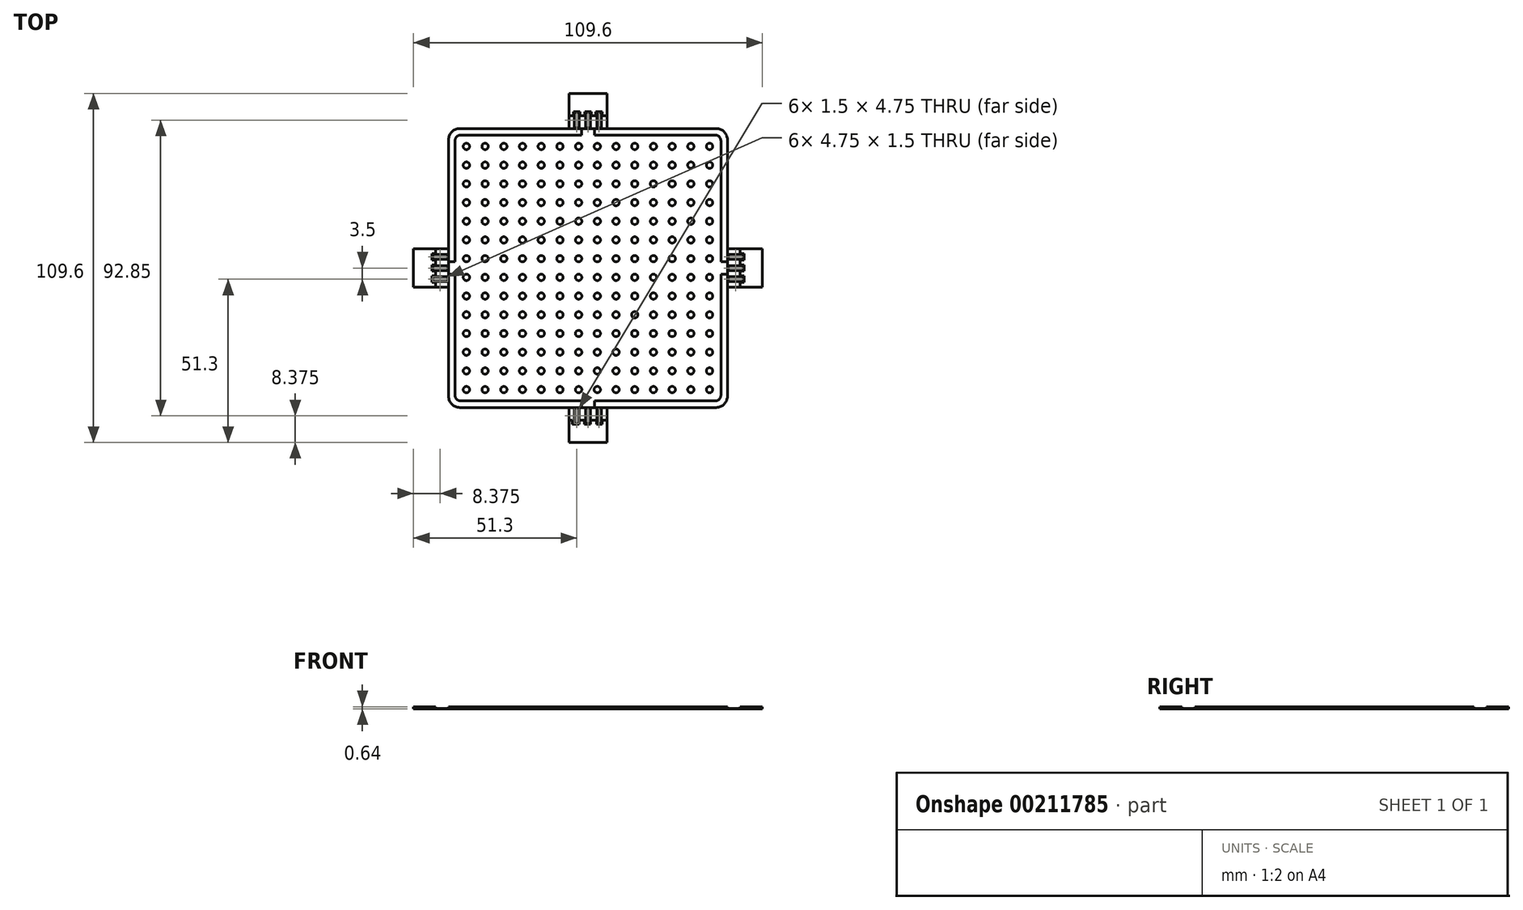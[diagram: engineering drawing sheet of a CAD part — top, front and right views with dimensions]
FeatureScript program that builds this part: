
annotation { "Feature Type Name" : "Feature", "Feature Type Description" : "" }
export const myFeature = defineFeature(function(context is Context, id is Id, definition is map)
    precondition{}
    {
        {
            var Q0;
            Q0=qCreatedBy(makeId("Top.planeOp"),FACE);
            var sketch = newSketch(context, id + "F0", { "sketchPlane" : qUnion([Q0])});
            skLineSegment(sketch, "E0.bottom", {"start": v(3.5, 87.6) * mm, "end": v(37.8, 87.6) * mm});
            skLineSegment(sketch, "E0.top", {"start": v(3.5, 0) * mm, "end": v(37.8, 0) * mm});
            skLineSegment(sketch, "E0.left", {"start": v(0, 84.1) * mm, "end": v(0, 49.8) * mm});
            skLineSegment(sketch, "E0.right", {"start": v(87.6, 84.1) * mm, "end": v(87.6, 49.8) * mm});
            skLineSegment(sketch, "E1", {"start": v(37.8, 87.6) * mm, "end": v(37.8, 98.6) * mm});
            skLineSegment(sketch, "E2", {"start": v(37.8, 98.6) * mm, "end": v(49.8, 98.6) * mm});
            skLineSegment(sketch, "E3", {"start": v(49.8, 98.6) * mm, "end": v(49.8, 87.6) * mm});
            skLineSegment(sketch, "E4.trimOffspring", {"start": v(49.8, 87.6) * mm, "end": v(84.1, 87.6) * mm});
            skLineSegment(sketch, "E5", {"start": v(87.6, 49.8) * mm, "end": v(98.6, 49.8) * mm});
            skLineSegment(sketch, "E6", {"start": v(98.6, 49.8) * mm, "end": v(98.6, 37.8) * mm});
            skLineSegment(sketch, "E7", {"start": v(98.6, 37.8) * mm, "end": v(87.6, 37.8) * mm});
            skLineSegment(sketch, "E8.trimOffspring", {"start": v(87.6, 37.8) * mm, "end": v(87.6, 3.5) * mm});
            skLineSegment(sketch, "E9", {"start": v(49.8, 0) * mm, "end": v(49.8, -11) * mm});
            skLineSegment(sketch, "E10", {"start": v(49.8, -11) * mm, "end": v(37.8, -11) * mm});
            skLineSegment(sketch, "E11", {"start": v(37.8, -11) * mm, "end": v(37.8, 0) * mm});
            skLineSegment(sketch, "E12.trimOffspring", {"start": v(49.8, 0) * mm, "end": v(84.1, 0) * mm});
            skLineSegment(sketch, "E13", {"start": v(0, 49.8) * mm, "end": v(-11, 49.8) * mm});
            skLineSegment(sketch, "E14", {"start": v(-11, 49.8) * mm, "end": v(-11, 37.8) * mm});
            skLineSegment(sketch, "E15", {"start": v(-11, 37.8) * mm, "end": v(0, 37.8) * mm});
            skLineSegment(sketch, "E16.trimOffspring", {"start": v(0, 37.8) * mm, "end": v(0, 3.5) * mm});
            skLineSegment(sketch, "E17.bottom", {"start": v(41.05, 87.85) * mm, "end": v(39.55, 87.85) * mm});
            skLineSegment(sketch, "E17.top", {"start": v(41.05, 92.6) * mm, "end": v(39.55, 92.6) * mm});
            skLineSegment(sketch, "E17.left", {"start": v(41.05, 87.85) * mm, "end": v(41.05, 92.6) * mm});
            skLineSegment(sketch, "E17.right", {"start": v(39.55, 87.85) * mm, "end": v(39.55, 92.6) * mm});
            skPoint(sketch, "E17.middle", {"position": v(40.3, 90.22) * mm});
            skLineSegment(sketch, "E18.1.0.0", {"start": v(44.55, 92.6) * mm, "end": v(43.05, 92.6) * mm});
            skLineSegment(sketch, "E18.1.0.1", {"start": v(44.55, 87.85) * mm, "end": v(44.55, 92.6) * mm});
            skLineSegment(sketch, "E18.1.0.2", {"start": v(44.55, 87.85) * mm, "end": v(43.05, 87.85) * mm});
            skLineSegment(sketch, "E18.1.0.3", {"start": v(43.05, 87.85) * mm, "end": v(43.05, 92.6) * mm});
            skPoint(sketch, "E18.1.0.4", {"position": v(43.8, 90.22) * mm});
            skLineSegment(sketch, "E18.2.0.0", {"start": v(48.05, 92.6) * mm, "end": v(46.55, 92.6) * mm});
            skLineSegment(sketch, "E18.2.0.1", {"start": v(48.05, 87.85) * mm, "end": v(48.05, 92.6) * mm});
            skLineSegment(sketch, "E18.2.0.2", {"start": v(48.05, 87.85) * mm, "end": v(46.55, 87.85) * mm});
            skLineSegment(sketch, "E18.2.0.3", {"start": v(46.55, 87.85) * mm, "end": v(46.55, 92.6) * mm});
            skPoint(sketch, "E18.2.0.4", {"position": v(47.3, 90.22) * mm});
            skLineSegment(sketch, "E18.direction1", {"start": v(39.55, 92.6) * mm, "end": v(43.05, 92.6) * mm, "construction": true});
            skLineSegment(sketch, "E19.bottom", {"start": v(92.6, 46.55) * mm, "end": v(87.85, 46.55) * mm});
            skLineSegment(sketch, "E19.top", {"start": v(92.6, 48.05) * mm, "end": v(87.85, 48.05) * mm});
            skLineSegment(sketch, "E19.left", {"start": v(92.6, 46.55) * mm, "end": v(92.6, 48.05) * mm});
            skLineSegment(sketch, "E19.right", {"start": v(87.85, 46.55) * mm, "end": v(87.85, 48.05) * mm});
            skPoint(sketch, "E19.middle", {"position": v(90.22, 47.3) * mm});
            skLineSegment(sketch, "E20.0.1.0", {"start": v(92.6, 43.05) * mm, "end": v(92.6, 44.55) * mm});
            skLineSegment(sketch, "E20.0.1.1", {"start": v(92.6, 44.55) * mm, "end": v(87.85, 44.55) * mm});
            skLineSegment(sketch, "E20.0.1.2", {"start": v(87.85, 43.05) * mm, "end": v(87.85, 44.55) * mm});
            skLineSegment(sketch, "E20.0.1.3", {"start": v(92.6, 43.05) * mm, "end": v(87.85, 43.05) * mm});
            skPoint(sketch, "E20.0.1.4", {"position": v(90.22, 43.8) * mm});
            skLineSegment(sketch, "E20.0.2.0", {"start": v(92.6, 39.55) * mm, "end": v(92.6, 41.05) * mm});
            skLineSegment(sketch, "E20.0.2.1", {"start": v(92.6, 41.05) * mm, "end": v(87.85, 41.05) * mm});
            skLineSegment(sketch, "E20.0.2.2", {"start": v(87.85, 39.55) * mm, "end": v(87.85, 41.05) * mm});
            skLineSegment(sketch, "E20.0.2.3", {"start": v(92.6, 39.55) * mm, "end": v(87.85, 39.55) * mm});
            skPoint(sketch, "E20.0.2.4", {"position": v(90.22, 40.3) * mm});
            skLineSegment(sketch, "E20.direction1", {"start": v(92.6, 46.55) * mm, "end": v(117.6, 46.55) * mm, "construction": true});
            skLineSegment(sketch, "E20.direction2", {"start": v(92.6, 46.55) * mm, "end": v(92.6, 43.05) * mm, "construction": true});
            skLineSegment(sketch, "E21.bottom", {"start": v(48.05, -5) * mm, "end": v(46.55, -5) * mm});
            skLineSegment(sketch, "E21.top", {"start": v(48.05, -0.25) * mm, "end": v(46.55, -0.25) * mm});
            skLineSegment(sketch, "E21.left", {"start": v(48.05, -5) * mm, "end": v(48.05, -0.25) * mm});
            skLineSegment(sketch, "E21.right", {"start": v(46.55, -5) * mm, "end": v(46.55, -0.25) * mm});
            skPoint(sketch, "E21.middle", {"position": v(47.3, -2.62) * mm});
            skLineSegment(sketch, "E22.1.0.0", {"start": v(44.55, -0.25) * mm, "end": v(43.05, -0.25) * mm});
            skLineSegment(sketch, "E22.1.0.1", {"start": v(44.55, -5) * mm, "end": v(44.55, -0.25) * mm});
            skLineSegment(sketch, "E22.1.0.2", {"start": v(44.55, -5) * mm, "end": v(43.05, -5) * mm});
            skLineSegment(sketch, "E22.1.0.3", {"start": v(43.05, -5) * mm, "end": v(43.05, -0.25) * mm});
            skPoint(sketch, "E22.1.0.4", {"position": v(43.8, -2.62) * mm});
            skLineSegment(sketch, "E22.2.0.0", {"start": v(41.05, -0.25) * mm, "end": v(39.55, -0.25) * mm});
            skLineSegment(sketch, "E22.2.0.1", {"start": v(41.05, -5) * mm, "end": v(41.05, -0.25) * mm});
            skLineSegment(sketch, "E22.2.0.2", {"start": v(41.05, -5) * mm, "end": v(39.55, -5) * mm});
            skLineSegment(sketch, "E22.2.0.3", {"start": v(39.55, -5) * mm, "end": v(39.55, -0.25) * mm});
            skPoint(sketch, "E22.2.0.4", {"position": v(40.3, -2.62) * mm});
            skLineSegment(sketch, "E22.direction1", {"start": v(46.55, -0.25) * mm, "end": v(43.05, -0.25) * mm, "construction": true});
            skLineSegment(sketch, "E23.bottom", {"start": v(-0.25, 46.55) * mm, "end": v(-5, 46.55) * mm});
            skLineSegment(sketch, "E23.top", {"start": v(-0.25, 48.05) * mm, "end": v(-5, 48.05) * mm});
            skLineSegment(sketch, "E23.left", {"start": v(-0.25, 46.55) * mm, "end": v(-0.25, 48.05) * mm});
            skLineSegment(sketch, "E23.right", {"start": v(-5, 46.55) * mm, "end": v(-5, 48.05) * mm});
            skPoint(sketch, "E23.middle", {"position": v(-2.63, 47.3) * mm});
            skLineSegment(sketch, "E24.0.1.0", {"start": v(-0.25, 43.05) * mm, "end": v(-0.25, 44.55) * mm});
            skLineSegment(sketch, "E24.0.1.1", {"start": v(-0.25, 44.55) * mm, "end": v(-5, 44.55) * mm});
            skLineSegment(sketch, "E24.0.1.2", {"start": v(-5, 43.05) * mm, "end": v(-5, 44.55) * mm});
            skPoint(sketch, "E24.0.1.3", {"position": v(-2.63, 43.8) * mm});
            skLineSegment(sketch, "E24.0.1.4", {"start": v(-0.25, 43.05) * mm, "end": v(-5, 43.05) * mm});
            skLineSegment(sketch, "E24.0.2.0", {"start": v(-0.25, 39.55) * mm, "end": v(-0.25, 41.05) * mm});
            skLineSegment(sketch, "E24.0.2.1", {"start": v(-0.25, 41.05) * mm, "end": v(-5, 41.05) * mm});
            skLineSegment(sketch, "E24.0.2.2", {"start": v(-5, 39.55) * mm, "end": v(-5, 41.05) * mm});
            skPoint(sketch, "E24.0.2.3", {"position": v(-2.63, 40.3) * mm});
            skLineSegment(sketch, "E24.0.2.4", {"start": v(-0.25, 39.55) * mm, "end": v(-5, 39.55) * mm});
            skLineSegment(sketch, "E24.direction1", {"start": v(-0.25, 46.55) * mm, "end": v(24.75, 46.55) * mm, "construction": true});
            skLineSegment(sketch, "E24.direction2", {"start": v(-0.25, 46.55) * mm, "end": v(-0.25, 43.05) * mm, "construction": true});
            skPoint(sketch, "E25.visualSharp", {"position": v(0, 87.6) * mm});
            skArc(sketch, "E25.filletArc", {"start": v(3.5, 87.6) * mm, "mid": v(1.03, 86.57) * mm, "end": v(0, 84.1) * mm});
            skPoint(sketch, "E26.visualSharp", {"position": v(87.6, 87.6) * mm});
            skArc(sketch, "E26.filletArc", {"start": v(87.6, 84.1) * mm, "mid": v(86.57, 86.57) * mm, "end": v(84.1, 87.6) * mm});
            skPoint(sketch, "E27.visualSharp", {"position": v(87.6, 0) * mm});
            skArc(sketch, "E27.filletArc", {"start": v(84.1, 0) * mm, "mid": v(86.57, 1.03) * mm, "end": v(87.6, 3.5) * mm});
            skPoint(sketch, "E28.visualSharp", {"position": v(0, 0) * mm});
            skArc(sketch, "E28.filletArc", {"start": v(0, 3.5) * mm, "mid": v(1.03, 1.03) * mm, "end": v(3.5, 0) * mm});
            skSolve(sketch);
        }
        {
            var Q0;
            Q0=makeQuery(id+"F0.imprint","IMPRINT",FACE,{"disambiguationData":[TD([[makeQuery(id+"F0.imprint","IMPRINT",EDGE,{"derivedFrom":sQuery(id+"F0.wireOp",EDGE,"E0.bottom")}),-1.0]])]});
            extrude(context, id + "F1", {"entities" : qUnion([Q0]), "oppositeDirection" : true, "depth" : .127 * mm});
        }
        {
            var Q0;
            Q0=qCreatedBy(makeId("Top.planeOp"),FACE);
            var sketch = newSketch(context, id + "F2", { "sketchPlane" : qUnion([Q0])});
            skCircle(sketch, "E29", {"center": v(5.61, 5.61) * mm, "radius": 1 * mm});
            skCircle(sketch, "E30.0.1.0", {"center": v(5.61, 11.49) * mm, "radius": 1 * mm});
            skCircle(sketch, "E30.0.2.0", {"center": v(5.61, 17.36) * mm, "radius": 1 * mm});
            skCircle(sketch, "E30.0.3.0", {"center": v(5.61, 23.24) * mm, "radius": 1 * mm});
            skCircle(sketch, "E30.0.4.0", {"center": v(5.61, 29.11) * mm, "radius": 1 * mm});
            skCircle(sketch, "E30.0.5.0", {"center": v(5.61, 34.99) * mm, "radius": 1 * mm});
            skCircle(sketch, "E30.0.6.0", {"center": v(5.61, 40.86) * mm, "radius": 1 * mm});
            skCircle(sketch, "E30.0.7.0", {"center": v(5.61, 46.74) * mm, "radius": 1 * mm});
            skCircle(sketch, "E30.0.8.0", {"center": v(5.61, 52.61) * mm, "radius": 1 * mm});
            skCircle(sketch, "E30.0.9.0", {"center": v(5.61, 58.49) * mm, "radius": 1 * mm});
            skCircle(sketch, "E30.0.10.0", {"center": v(5.61, 64.36) * mm, "radius": 1 * mm});
            skCircle(sketch, "E30.0.11.0", {"center": v(5.61, 70.24) * mm, "radius": 1 * mm});
            skCircle(sketch, "E30.0.12.0", {"center": v(5.61, 76.11) * mm, "radius": 1 * mm});
            skCircle(sketch, "E30.0.13.0", {"center": v(5.61, 81.99) * mm, "radius": 1 * mm});
            skCircle(sketch, "E30.1.0.0", {"center": v(11.49, 5.61) * mm, "radius": 1 * mm});
            skCircle(sketch, "E30.1.1.0", {"center": v(11.49, 11.49) * mm, "radius": 1 * mm});
            skCircle(sketch, "E30.1.2.0", {"center": v(11.49, 17.36) * mm, "radius": 1 * mm});
            skCircle(sketch, "E30.1.3.0", {"center": v(11.49, 23.24) * mm, "radius": 1 * mm});
            skCircle(sketch, "E30.1.4.0", {"center": v(11.49, 29.11) * mm, "radius": 1 * mm});
            skCircle(sketch, "E30.1.5.0", {"center": v(11.49, 34.99) * mm, "radius": 1 * mm});
            skCircle(sketch, "E30.1.6.0", {"center": v(11.49, 40.86) * mm, "radius": 1 * mm});
            skCircle(sketch, "E30.1.7.0", {"center": v(11.49, 46.74) * mm, "radius": 1 * mm});
            skCircle(sketch, "E30.1.8.0", {"center": v(11.49, 52.61) * mm, "radius": 1 * mm});
            skCircle(sketch, "E30.1.9.0", {"center": v(11.49, 58.49) * mm, "radius": 1 * mm});
            skCircle(sketch, "E30.1.10.0", {"center": v(11.49, 64.36) * mm, "radius": 1 * mm});
            skCircle(sketch, "E30.1.11.0", {"center": v(11.49, 70.24) * mm, "radius": 1 * mm});
            skCircle(sketch, "E30.1.12.0", {"center": v(11.49, 76.11) * mm, "radius": 1 * mm});
            skCircle(sketch, "E30.1.13.0", {"center": v(11.49, 81.99) * mm, "radius": 1 * mm});
            skCircle(sketch, "E30.2.0.0", {"center": v(17.36, 5.61) * mm, "radius": 1 * mm});
            skCircle(sketch, "E30.2.1.0", {"center": v(17.36, 11.49) * mm, "radius": 1 * mm});
            skCircle(sketch, "E30.2.2.0", {"center": v(17.36, 17.36) * mm, "radius": 1 * mm});
            skCircle(sketch, "E30.2.3.0", {"center": v(17.36, 23.24) * mm, "radius": 1 * mm});
            skCircle(sketch, "E30.2.4.0", {"center": v(17.36, 29.11) * mm, "radius": 1 * mm});
            skCircle(sketch, "E30.2.5.0", {"center": v(17.36, 34.99) * mm, "radius": 1 * mm});
            skCircle(sketch, "E30.2.6.0", {"center": v(17.36, 40.86) * mm, "radius": 1 * mm});
            skCircle(sketch, "E30.2.7.0", {"center": v(17.36, 46.74) * mm, "radius": 1 * mm});
            skCircle(sketch, "E30.2.8.0", {"center": v(17.36, 52.61) * mm, "radius": 1 * mm});
            skCircle(sketch, "E30.2.9.0", {"center": v(17.36, 58.49) * mm, "radius": 1 * mm});
            skCircle(sketch, "E30.2.10.0", {"center": v(17.36, 64.36) * mm, "radius": 1 * mm});
            skCircle(sketch, "E30.2.11.0", {"center": v(17.36, 70.24) * mm, "radius": 1 * mm});
            skCircle(sketch, "E30.2.12.0", {"center": v(17.36, 76.11) * mm, "radius": 1 * mm});
            skCircle(sketch, "E30.2.13.0", {"center": v(17.36, 81.99) * mm, "radius": 1 * mm});
            skCircle(sketch, "E30.3.0.0", {"center": v(23.24, 5.61) * mm, "radius": 1 * mm});
            skCircle(sketch, "E30.3.1.0", {"center": v(23.24, 11.49) * mm, "radius": 1 * mm});
            skCircle(sketch, "E30.3.2.0", {"center": v(23.24, 17.36) * mm, "radius": 1 * mm});
            skCircle(sketch, "E30.3.3.0", {"center": v(23.24, 23.24) * mm, "radius": 1 * mm});
            skCircle(sketch, "E30.3.4.0", {"center": v(23.24, 29.11) * mm, "radius": 1 * mm});
            skCircle(sketch, "E30.3.5.0", {"center": v(23.24, 34.99) * mm, "radius": 1 * mm});
            skCircle(sketch, "E30.3.6.0", {"center": v(23.24, 40.86) * mm, "radius": 1 * mm});
            skCircle(sketch, "E30.3.7.0", {"center": v(23.24, 46.74) * mm, "radius": 1 * mm});
            skCircle(sketch, "E30.3.8.0", {"center": v(23.24, 52.61) * mm, "radius": 1 * mm});
            skCircle(sketch, "E30.3.9.0", {"center": v(23.24, 58.49) * mm, "radius": 1 * mm});
            skCircle(sketch, "E30.3.10.0", {"center": v(23.24, 64.36) * mm, "radius": 1 * mm});
            skCircle(sketch, "E30.3.11.0", {"center": v(23.24, 70.24) * mm, "radius": 1 * mm});
            skCircle(sketch, "E30.3.12.0", {"center": v(23.24, 76.11) * mm, "radius": 1 * mm});
            skCircle(sketch, "E30.3.13.0", {"center": v(23.24, 81.99) * mm, "radius": 1 * mm});
            skCircle(sketch, "E30.4.0.0", {"center": v(29.11, 5.61) * mm, "radius": 1 * mm});
            skCircle(sketch, "E30.4.1.0", {"center": v(29.11, 11.49) * mm, "radius": 1 * mm});
            skCircle(sketch, "E30.4.2.0", {"center": v(29.11, 17.36) * mm, "radius": 1 * mm});
            skCircle(sketch, "E30.4.3.0", {"center": v(29.11, 23.24) * mm, "radius": 1 * mm});
            skCircle(sketch, "E30.4.4.0", {"center": v(29.11, 29.11) * mm, "radius": 1 * mm});
            skCircle(sketch, "E30.4.5.0", {"center": v(29.11, 34.99) * mm, "radius": 1 * mm});
            skCircle(sketch, "E30.4.6.0", {"center": v(29.11, 40.86) * mm, "radius": 1 * mm});
            skCircle(sketch, "E30.4.7.0", {"center": v(29.11, 46.74) * mm, "radius": 1 * mm});
            skCircle(sketch, "E30.4.8.0", {"center": v(29.11, 52.61) * mm, "radius": 1 * mm});
            skCircle(sketch, "E30.4.9.0", {"center": v(29.11, 58.49) * mm, "radius": 1 * mm});
            skCircle(sketch, "E30.4.10.0", {"center": v(29.11, 64.36) * mm, "radius": 1 * mm});
            skCircle(sketch, "E30.4.11.0", {"center": v(29.11, 70.24) * mm, "radius": 1 * mm});
            skCircle(sketch, "E30.4.12.0", {"center": v(29.11, 76.11) * mm, "radius": 1 * mm});
            skCircle(sketch, "E30.4.13.0", {"center": v(29.11, 81.99) * mm, "radius": 1 * mm});
            skCircle(sketch, "E30.5.0.0", {"center": v(34.99, 5.61) * mm, "radius": 1 * mm});
            skCircle(sketch, "E30.5.1.0", {"center": v(34.99, 11.49) * mm, "radius": 1 * mm});
            skCircle(sketch, "E30.5.2.0", {"center": v(34.99, 17.36) * mm, "radius": 1 * mm});
            skCircle(sketch, "E30.5.3.0", {"center": v(34.99, 23.24) * mm, "radius": 1 * mm});
            skCircle(sketch, "E30.5.4.0", {"center": v(34.99, 29.11) * mm, "radius": 1 * mm});
            skCircle(sketch, "E30.5.5.0", {"center": v(34.99, 34.99) * mm, "radius": 1 * mm});
            skCircle(sketch, "E30.5.6.0", {"center": v(34.99, 40.86) * mm, "radius": 1 * mm});
            skCircle(sketch, "E30.5.7.0", {"center": v(34.99, 46.74) * mm, "radius": 1 * mm});
            skCircle(sketch, "E30.5.8.0", {"center": v(34.99, 52.61) * mm, "radius": 1 * mm});
            skCircle(sketch, "E30.5.9.0", {"center": v(34.99, 58.49) * mm, "radius": 1 * mm});
            skCircle(sketch, "E30.5.10.0", {"center": v(34.99, 64.36) * mm, "radius": 1 * mm});
            skCircle(sketch, "E30.5.11.0", {"center": v(34.99, 70.24) * mm, "radius": 1 * mm});
            skCircle(sketch, "E30.5.12.0", {"center": v(34.99, 76.11) * mm, "radius": 1 * mm});
            skCircle(sketch, "E30.5.13.0", {"center": v(34.99, 81.99) * mm, "radius": 1 * mm});
            skCircle(sketch, "E30.6.0.0", {"center": v(40.86, 5.61) * mm, "radius": 1 * mm});
            skCircle(sketch, "E30.6.1.0", {"center": v(40.86, 11.49) * mm, "radius": 1 * mm});
            skCircle(sketch, "E30.6.2.0", {"center": v(40.86, 17.36) * mm, "radius": 1 * mm});
            skCircle(sketch, "E30.6.3.0", {"center": v(40.86, 23.24) * mm, "radius": 1 * mm});
            skCircle(sketch, "E30.6.4.0", {"center": v(40.86, 29.11) * mm, "radius": 1 * mm});
            skCircle(sketch, "E30.6.5.0", {"center": v(40.86, 34.99) * mm, "radius": 1 * mm});
            skCircle(sketch, "E30.6.6.0", {"center": v(40.86, 40.86) * mm, "radius": 1 * mm});
            skCircle(sketch, "E30.6.7.0", {"center": v(40.86, 46.74) * mm, "radius": 1 * mm});
            skCircle(sketch, "E30.6.8.0", {"center": v(40.86, 52.61) * mm, "radius": 1 * mm});
            skCircle(sketch, "E30.6.9.0", {"center": v(40.86, 58.49) * mm, "radius": 1 * mm});
            skCircle(sketch, "E30.6.10.0", {"center": v(40.86, 64.36) * mm, "radius": 1 * mm});
            skCircle(sketch, "E30.6.11.0", {"center": v(40.86, 70.24) * mm, "radius": 1 * mm});
            skCircle(sketch, "E30.6.12.0", {"center": v(40.86, 76.11) * mm, "radius": 1 * mm});
            skCircle(sketch, "E30.6.13.0", {"center": v(40.86, 81.99) * mm, "radius": 1 * mm});
            skCircle(sketch, "E30.7.0.0", {"center": v(46.74, 5.61) * mm, "radius": 1 * mm});
            skCircle(sketch, "E30.7.1.0", {"center": v(46.74, 11.49) * mm, "radius": 1 * mm});
            skCircle(sketch, "E30.7.2.0", {"center": v(46.74, 17.36) * mm, "radius": 1 * mm});
            skCircle(sketch, "E30.7.3.0", {"center": v(46.74, 23.24) * mm, "radius": 1 * mm});
            skCircle(sketch, "E30.7.4.0", {"center": v(46.74, 29.11) * mm, "radius": 1 * mm});
            skCircle(sketch, "E30.7.5.0", {"center": v(46.74, 34.99) * mm, "radius": 1 * mm});
            skCircle(sketch, "E30.7.6.0", {"center": v(46.74, 40.86) * mm, "radius": 1 * mm});
            skCircle(sketch, "E30.7.7.0", {"center": v(46.74, 46.74) * mm, "radius": 1 * mm});
            skCircle(sketch, "E30.7.8.0", {"center": v(46.74, 52.61) * mm, "radius": 1 * mm});
            skCircle(sketch, "E30.7.9.0", {"center": v(46.74, 58.49) * mm, "radius": 1 * mm});
            skCircle(sketch, "E30.7.10.0", {"center": v(46.74, 64.36) * mm, "radius": 1 * mm});
            skCircle(sketch, "E30.7.11.0", {"center": v(46.74, 70.24) * mm, "radius": 1 * mm});
            skCircle(sketch, "E30.7.12.0", {"center": v(46.74, 76.11) * mm, "radius": 1 * mm});
            skCircle(sketch, "E30.7.13.0", {"center": v(46.74, 81.99) * mm, "radius": 1 * mm});
            skCircle(sketch, "E30.8.0.0", {"center": v(52.61, 5.61) * mm, "radius": 1 * mm});
            skCircle(sketch, "E30.8.1.0", {"center": v(52.61, 11.49) * mm, "radius": 1 * mm});
            skCircle(sketch, "E30.8.2.0", {"center": v(52.61, 17.36) * mm, "radius": 1 * mm});
            skCircle(sketch, "E30.8.3.0", {"center": v(52.61, 23.24) * mm, "radius": 1 * mm});
            skCircle(sketch, "E30.8.4.0", {"center": v(52.61, 29.11) * mm, "radius": 1 * mm});
            skCircle(sketch, "E30.8.5.0", {"center": v(52.61, 34.99) * mm, "radius": 1 * mm});
            skCircle(sketch, "E30.8.6.0", {"center": v(52.61, 40.86) * mm, "radius": 1 * mm});
            skCircle(sketch, "E30.8.7.0", {"center": v(52.61, 46.74) * mm, "radius": 1 * mm});
            skCircle(sketch, "E30.8.8.0", {"center": v(52.61, 52.61) * mm, "radius": 1 * mm});
            skCircle(sketch, "E30.8.9.0", {"center": v(52.61, 58.49) * mm, "radius": 1 * mm});
            skCircle(sketch, "E30.8.10.0", {"center": v(52.61, 64.36) * mm, "radius": 1 * mm});
            skCircle(sketch, "E30.8.11.0", {"center": v(52.61, 70.24) * mm, "radius": 1 * mm});
            skCircle(sketch, "E30.8.12.0", {"center": v(52.61, 76.11) * mm, "radius": 1 * mm});
            skCircle(sketch, "E30.8.13.0", {"center": v(52.61, 81.99) * mm, "radius": 1 * mm});
            skCircle(sketch, "E30.9.0.0", {"center": v(58.49, 5.61) * mm, "radius": 1 * mm});
            skCircle(sketch, "E30.9.1.0", {"center": v(58.49, 11.49) * mm, "radius": 1 * mm});
            skCircle(sketch, "E30.9.2.0", {"center": v(58.49, 17.36) * mm, "radius": 1 * mm});
            skCircle(sketch, "E30.9.3.0", {"center": v(58.49, 23.24) * mm, "radius": 1 * mm});
            skCircle(sketch, "E30.9.4.0", {"center": v(58.49, 29.11) * mm, "radius": 1 * mm});
            skCircle(sketch, "E30.9.5.0", {"center": v(58.49, 34.99) * mm, "radius": 1 * mm});
            skCircle(sketch, "E30.9.6.0", {"center": v(58.49, 40.86) * mm, "radius": 1 * mm});
            skCircle(sketch, "E30.9.7.0", {"center": v(58.49, 46.74) * mm, "radius": 1 * mm});
            skCircle(sketch, "E30.9.8.0", {"center": v(58.49, 52.61) * mm, "radius": 1 * mm});
            skCircle(sketch, "E30.9.9.0", {"center": v(58.49, 58.49) * mm, "radius": 1 * mm});
            skCircle(sketch, "E30.9.10.0", {"center": v(58.49, 64.36) * mm, "radius": 1 * mm});
            skCircle(sketch, "E30.9.11.0", {"center": v(58.49, 70.24) * mm, "radius": 1 * mm});
            skCircle(sketch, "E30.9.12.0", {"center": v(58.49, 76.11) * mm, "radius": 1 * mm});
            skCircle(sketch, "E30.9.13.0", {"center": v(58.49, 81.99) * mm, "radius": 1 * mm});
            skCircle(sketch, "E30.10.0.0", {"center": v(64.36, 5.61) * mm, "radius": 1 * mm});
            skCircle(sketch, "E30.10.1.0", {"center": v(64.36, 11.49) * mm, "radius": 1 * mm});
            skCircle(sketch, "E30.10.2.0", {"center": v(64.36, 17.36) * mm, "radius": 1 * mm});
            skCircle(sketch, "E30.10.3.0", {"center": v(64.36, 23.24) * mm, "radius": 1 * mm});
            skCircle(sketch, "E30.10.4.0", {"center": v(64.36, 29.11) * mm, "radius": 1 * mm});
            skCircle(sketch, "E30.10.5.0", {"center": v(64.36, 34.99) * mm, "radius": 1 * mm});
            skCircle(sketch, "E30.10.6.0", {"center": v(64.36, 40.86) * mm, "radius": 1 * mm});
            skCircle(sketch, "E30.10.7.0", {"center": v(64.36, 46.74) * mm, "radius": 1 * mm});
            skCircle(sketch, "E30.10.8.0", {"center": v(64.36, 52.61) * mm, "radius": 1 * mm});
            skCircle(sketch, "E30.10.9.0", {"center": v(64.36, 58.49) * mm, "radius": 1 * mm});
            skCircle(sketch, "E30.10.10.0", {"center": v(64.36, 64.36) * mm, "radius": 1 * mm});
            skCircle(sketch, "E30.10.11.0", {"center": v(64.36, 70.24) * mm, "radius": 1 * mm});
            skCircle(sketch, "E30.10.12.0", {"center": v(64.36, 76.11) * mm, "radius": 1 * mm});
            skCircle(sketch, "E30.10.13.0", {"center": v(64.36, 81.99) * mm, "radius": 1 * mm});
            skCircle(sketch, "E30.11.0.0", {"center": v(70.24, 5.61) * mm, "radius": 1 * mm});
            skCircle(sketch, "E30.11.1.0", {"center": v(70.24, 11.49) * mm, "radius": 1 * mm});
            skCircle(sketch, "E30.11.2.0", {"center": v(70.24, 17.36) * mm, "radius": 1 * mm});
            skCircle(sketch, "E30.11.3.0", {"center": v(70.24, 23.24) * mm, "radius": 1 * mm});
            skCircle(sketch, "E30.11.4.0", {"center": v(70.24, 29.11) * mm, "radius": 1 * mm});
            skCircle(sketch, "E30.11.5.0", {"center": v(70.24, 34.99) * mm, "radius": 1 * mm});
            skCircle(sketch, "E30.11.6.0", {"center": v(70.24, 40.86) * mm, "radius": 1 * mm});
            skCircle(sketch, "E30.11.7.0", {"center": v(70.24, 46.74) * mm, "radius": 1 * mm});
            skCircle(sketch, "E30.11.8.0", {"center": v(70.24, 52.61) * mm, "radius": 1 * mm});
            skCircle(sketch, "E30.11.9.0", {"center": v(70.24, 58.49) * mm, "radius": 1 * mm});
            skCircle(sketch, "E30.11.10.0", {"center": v(70.24, 64.36) * mm, "radius": 1 * mm});
            skCircle(sketch, "E30.11.11.0", {"center": v(70.24, 70.24) * mm, "radius": 1 * mm});
            skCircle(sketch, "E30.11.12.0", {"center": v(70.24, 76.11) * mm, "radius": 1 * mm});
            skCircle(sketch, "E30.11.13.0", {"center": v(70.24, 81.99) * mm, "radius": 1 * mm});
            skCircle(sketch, "E30.12.0.0", {"center": v(76.11, 5.61) * mm, "radius": 1 * mm});
            skCircle(sketch, "E30.12.1.0", {"center": v(76.11, 11.49) * mm, "radius": 1 * mm});
            skCircle(sketch, "E30.12.2.0", {"center": v(76.11, 17.36) * mm, "radius": 1 * mm});
            skCircle(sketch, "E30.12.3.0", {"center": v(76.11, 23.24) * mm, "radius": 1 * mm});
            skCircle(sketch, "E30.12.4.0", {"center": v(76.11, 29.11) * mm, "radius": 1 * mm});
            skCircle(sketch, "E30.12.5.0", {"center": v(76.11, 34.99) * mm, "radius": 1 * mm});
            skCircle(sketch, "E30.12.6.0", {"center": v(76.11, 40.86) * mm, "radius": 1 * mm});
            skCircle(sketch, "E30.12.7.0", {"center": v(76.11, 46.74) * mm, "radius": 1 * mm});
            skCircle(sketch, "E30.12.8.0", {"center": v(76.11, 52.61) * mm, "radius": 1 * mm});
            skCircle(sketch, "E30.12.9.0", {"center": v(76.11, 58.49) * mm, "radius": 1 * mm});
            skCircle(sketch, "E30.12.10.0", {"center": v(76.11, 64.36) * mm, "radius": 1 * mm});
            skCircle(sketch, "E30.12.11.0", {"center": v(76.11, 70.24) * mm, "radius": 1 * mm});
            skCircle(sketch, "E30.12.12.0", {"center": v(76.11, 76.11) * mm, "radius": 1 * mm});
            skCircle(sketch, "E30.12.13.0", {"center": v(76.11, 81.99) * mm, "radius": 1 * mm});
            skCircle(sketch, "E30.13.0.0", {"center": v(81.99, 5.61) * mm, "radius": 1 * mm});
            skCircle(sketch, "E30.13.1.0", {"center": v(81.99, 11.49) * mm, "radius": 1 * mm});
            skCircle(sketch, "E30.13.2.0", {"center": v(81.99, 17.36) * mm, "radius": 1 * mm});
            skCircle(sketch, "E30.13.3.0", {"center": v(81.99, 23.24) * mm, "radius": 1 * mm});
            skCircle(sketch, "E30.13.4.0", {"center": v(81.99, 29.11) * mm, "radius": 1 * mm});
            skCircle(sketch, "E30.13.5.0", {"center": v(81.99, 34.99) * mm, "radius": 1 * mm});
            skCircle(sketch, "E30.13.6.0", {"center": v(81.99, 40.86) * mm, "radius": 1 * mm});
            skCircle(sketch, "E30.13.7.0", {"center": v(81.99, 46.74) * mm, "radius": 1 * mm});
            skCircle(sketch, "E30.13.8.0", {"center": v(81.99, 52.61) * mm, "radius": 1 * mm});
            skCircle(sketch, "E30.13.9.0", {"center": v(81.99, 58.49) * mm, "radius": 1 * mm});
            skCircle(sketch, "E30.13.10.0", {"center": v(81.99, 64.36) * mm, "radius": 1 * mm});
            skCircle(sketch, "E30.13.11.0", {"center": v(81.99, 70.24) * mm, "radius": 1 * mm});
            skCircle(sketch, "E30.13.12.0", {"center": v(81.99, 76.11) * mm, "radius": 1 * mm});
            skCircle(sketch, "E30.13.13.0", {"center": v(81.99, 81.99) * mm, "radius": 1 * mm});
            skLineSegment(sketch, "E30.direction1", {"start": v(5.61, 5.61) * mm, "end": v(11.49, 5.61) * mm, "construction": true});
            skLineSegment(sketch, "E30.direction2", {"start": v(5.61, 5.61) * mm, "end": v(5.61, 11.49) * mm, "construction": true});
            skSolve(sketch);
        }
        {
            var Q0;
            Q0=makeQuery(id+"F2.imprint","IMPRINT",FACE,{"disambiguationData":[TD([[makeQuery(id+"F2.imprint","IMPRINT",EDGE,{"derivedFrom":sQuery(id+"F2.wireOp",EDGE,"E30.0.5.0")}),1.0]])]});
            var Q1;
            Q1=makeQuery(id+"F2.imprint","IMPRINT",FACE,{"disambiguationData":[TD([[makeQuery(id+"F2.imprint","IMPRINT",EDGE,{"derivedFrom":sQuery(id+"F2.wireOp",EDGE,"E30.13.9.0")}),1.0]])]});
            var Q2;
            Q2=makeQuery(id+"F2.imprint","IMPRINT",FACE,{"disambiguationData":[TD([[makeQuery(id+"F2.imprint","IMPRINT",EDGE,{"derivedFrom":sQuery(id+"F2.wireOp",EDGE,"E30.3.5.0")}),1.0]])]});
            var Q3;
            Q3=makeQuery(id+"F2.imprint","IMPRINT",FACE,{"disambiguationData":[TD([[makeQuery(id+"F2.imprint","IMPRINT",EDGE,{"derivedFrom":sQuery(id+"F2.wireOp",EDGE,"E30.2.3.0")}),1.0]])]});
            var Q4;
            Q4=makeQuery(id+"F2.imprint","IMPRINT",FACE,{"disambiguationData":[TD([[makeQuery(id+"F2.imprint","IMPRINT",EDGE,{"derivedFrom":sQuery(id+"F2.wireOp",EDGE,"E30.7.13.0")}),1.0]])]});
            var Q5;
            Q5=makeQuery(id+"F2.imprint","IMPRINT",FACE,{"disambiguationData":[TD([[makeQuery(id+"F2.imprint","IMPRINT",EDGE,{"derivedFrom":sQuery(id+"F2.wireOp",EDGE,"E30.6.11.0")}),1.0]])]});
            var Q6;
            Q6=makeQuery(id+"F2.imprint","IMPRINT",FACE,{"disambiguationData":[TD([[makeQuery(id+"F2.imprint","IMPRINT",EDGE,{"derivedFrom":sQuery(id+"F2.wireOp",EDGE,"E30.5.9.0")}),1.0]])]});
            var Q7;
            Q7=makeQuery(id+"F2.imprint","IMPRINT",FACE,{"disambiguationData":[TD([[makeQuery(id+"F2.imprint","IMPRINT",EDGE,{"derivedFrom":sQuery(id+"F2.wireOp",EDGE,"E30.4.7.0")}),1.0]])]});
            var Q8;
            Q8=makeQuery(id+"F2.imprint","IMPRINT",FACE,{"disambiguationData":[TD([[makeQuery(id+"F2.imprint","IMPRINT",EDGE,{"derivedFrom":sQuery(id+"F2.wireOp",EDGE,"E30.12.7.0")}),1.0]])]});
            var Q9;
            Q9=makeQuery(id+"F2.imprint","IMPRINT",FACE,{"disambiguationData":[TD([[makeQuery(id+"F2.imprint","IMPRINT",EDGE,{"derivedFrom":sQuery(id+"F2.wireOp",EDGE,"E30.11.5.0")}),1.0]])]});
            var Q10;
            Q10=makeQuery(id+"F2.imprint","IMPRINT",FACE,{"disambiguationData":[TD([[makeQuery(id+"F2.imprint","IMPRINT",EDGE,{"derivedFrom":sQuery(id+"F2.wireOp",EDGE,"E30.10.3.0")}),1.0]])]});
            var Q11;
            Q11=makeQuery(id+"F2.imprint","IMPRINT",FACE,{"disambiguationData":[TD([[makeQuery(id+"F2.imprint","IMPRINT",EDGE,{"derivedFrom":sQuery(id+"F2.wireOp",EDGE,"E30.9.1.0")}),1.0]])]});
            var Q12;
            Q12=makeQuery(id+"F2.imprint","IMPRINT",FACE,{"disambiguationData":[TD([[makeQuery(id+"F2.imprint","IMPRINT",EDGE,{"derivedFrom":sQuery(id+"F2.wireOp",EDGE,"E30.2.1.0")}),1.0]])]});
            var Q13;
            Q13=makeQuery(id+"F2.imprint","IMPRINT",FACE,{"disambiguationData":[TD([[makeQuery(id+"F2.imprint","IMPRINT",EDGE,{"derivedFrom":sQuery(id+"F2.wireOp",EDGE,"E30.6.9.0")}),1.0]])]});
            var Q14;
            Q14=makeQuery(id+"F2.imprint","IMPRINT",FACE,{"disambiguationData":[TD([[makeQuery(id+"F2.imprint","IMPRINT",EDGE,{"derivedFrom":sQuery(id+"F2.wireOp",EDGE,"E30.5.7.0")}),1.0]])]});
            var Q15;
            Q15=makeQuery(id+"F2.imprint","IMPRINT",FACE,{"disambiguationData":[TD([[makeQuery(id+"F2.imprint","IMPRINT",EDGE,{"derivedFrom":sQuery(id+"F2.wireOp",EDGE,"E30.4.5.0")}),1.0]])]});
            var Q16;
            Q16=makeQuery(id+"F2.imprint","IMPRINT",FACE,{"disambiguationData":[TD([[makeQuery(id+"F2.imprint","IMPRINT",EDGE,{"derivedFrom":sQuery(id+"F2.wireOp",EDGE,"E30.3.3.0")}),1.0]])]});
            var Q17;
            Q17=makeQuery(id+"F2.imprint","IMPRINT",FACE,{"disambiguationData":[TD([[makeQuery(id+"F2.imprint","IMPRINT",EDGE,{"derivedFrom":sQuery(id+"F2.wireOp",EDGE,"E30.11.3.0")}),1.0]])]});
            var Q18;
            Q18=makeQuery(id+"F2.imprint","IMPRINT",FACE,{"disambiguationData":[TD([[makeQuery(id+"F2.imprint","IMPRINT",EDGE,{"derivedFrom":sQuery(id+"F2.wireOp",EDGE,"E30.10.1.0")}),1.0]])]});
            var Q19;
            Q19=makeQuery(id+"F2.imprint","IMPRINT",FACE,{"disambiguationData":[TD([[makeQuery(id+"F2.imprint","IMPRINT",EDGE,{"derivedFrom":sQuery(id+"F2.wireOp",EDGE,"E30.8.13.0")}),1.0]])]});
            var Q20;
            Q20=makeQuery(id+"F2.imprint","IMPRINT",FACE,{"disambiguationData":[TD([[makeQuery(id+"F2.imprint","IMPRINT",EDGE,{"derivedFrom":sQuery(id+"F2.wireOp",EDGE,"E30.7.11.0")}),1.0]])]});
            var Q21;
            Q21=makeQuery(id+"F2.imprint","IMPRINT",FACE,{"disambiguationData":[TD([[makeQuery(id+"F2.imprint","IMPRINT",EDGE,{"derivedFrom":sQuery(id+"F2.wireOp",EDGE,"E30.13.7.0")}),1.0]])]});
            var Q22;
            Q22=makeQuery(id+"F2.imprint","IMPRINT",FACE,{"disambiguationData":[TD([[makeQuery(id+"F2.imprint","IMPRINT",EDGE,{"derivedFrom":sQuery(id+"F2.wireOp",EDGE,"E30.12.5.0")}),1.0]])]});
            var Q23;
            Q23=makeQuery(id+"F2.imprint","IMPRINT",FACE,{"disambiguationData":[TD([[makeQuery(id+"F2.imprint","IMPRINT",EDGE,{"derivedFrom":sQuery(id+"F2.wireOp",EDGE,"E30.2.2.0")}),1.0]])]});
            var Q24;
            Q24=makeQuery(id+"F2.imprint","IMPRINT",FACE,{"disambiguationData":[TD([[makeQuery(id+"F2.imprint","IMPRINT",EDGE,{"derivedFrom":sQuery(id+"F2.wireOp",EDGE,"E30.6.10.0")}),1.0]])]});
            var Q25;
            Q25=makeQuery(id+"F2.imprint","IMPRINT",FACE,{"disambiguationData":[TD([[makeQuery(id+"F2.imprint","IMPRINT",EDGE,{"derivedFrom":sQuery(id+"F2.wireOp",EDGE,"E30.5.8.0")}),1.0]])]});
            var Q26;
            Q26=makeQuery(id+"F2.imprint","IMPRINT",FACE,{"disambiguationData":[TD([[makeQuery(id+"F2.imprint","IMPRINT",EDGE,{"derivedFrom":sQuery(id+"F2.wireOp",EDGE,"E30.4.6.0")}),1.0]])]});
            var Q27;
            Q27=makeQuery(id+"F2.imprint","IMPRINT",FACE,{"disambiguationData":[TD([[makeQuery(id+"F2.imprint","IMPRINT",EDGE,{"derivedFrom":sQuery(id+"F2.wireOp",EDGE,"E30.3.4.0")}),1.0]])]});
            var Q28;
            Q28=makeQuery(id+"F2.imprint","IMPRINT",FACE,{"disambiguationData":[TD([[makeQuery(id+"F2.imprint","IMPRINT",EDGE,{"derivedFrom":sQuery(id+"F2.wireOp",EDGE,"E30.11.4.0")}),1.0]])]});
            var Q29;
            Q29=makeQuery(id+"F2.imprint","IMPRINT",FACE,{"disambiguationData":[TD([[makeQuery(id+"F2.imprint","IMPRINT",EDGE,{"derivedFrom":sQuery(id+"F2.wireOp",EDGE,"E30.10.2.0")}),1.0]])]});
            var Q30;
            Q30=makeQuery(id+"F2.imprint","IMPRINT",FACE,{"disambiguationData":[TD([[makeQuery(id+"F2.imprint","IMPRINT",EDGE,{"derivedFrom":sQuery(id+"F2.wireOp",EDGE,"E30.9.0.0")}),1.0]])]});
            var Q31;
            Q31=makeQuery(id+"F2.imprint","IMPRINT",FACE,{"disambiguationData":[TD([[makeQuery(id+"F2.imprint","IMPRINT",EDGE,{"derivedFrom":sQuery(id+"F2.wireOp",EDGE,"E30.7.12.0")}),1.0]])]});
            var Q32;
            Q32=makeQuery(id+"F2.imprint","IMPRINT",FACE,{"disambiguationData":[TD([[makeQuery(id+"F2.imprint","IMPRINT",EDGE,{"derivedFrom":sQuery(id+"F2.wireOp",EDGE,"E30.13.8.0")}),1.0]])]});
            var Q33;
            Q33=makeQuery(id+"F2.imprint","IMPRINT",FACE,{"disambiguationData":[TD([[makeQuery(id+"F2.imprint","IMPRINT",EDGE,{"derivedFrom":sQuery(id+"F2.wireOp",EDGE,"E30.12.6.0")}),1.0]])]});
            var Q34;
            Q34=makeQuery(id+"F2.imprint","IMPRINT",FACE,{"disambiguationData":[TD([[makeQuery(id+"F2.imprint","IMPRINT",EDGE,{"derivedFrom":sQuery(id+"F2.wireOp",EDGE,"E30.2.4.0")}),1.0]])]});
            var Q35;
            Q35=makeQuery(id+"F2.imprint","IMPRINT",FACE,{"disambiguationData":[TD([[makeQuery(id+"F2.imprint","IMPRINT",EDGE,{"derivedFrom":sQuery(id+"F2.wireOp",EDGE,"E30.1.2.0")}),1.0]])]});
            var Q36;
            Q36=makeQuery(id+"F2.imprint","IMPRINT",FACE,{"disambiguationData":[TD([[makeQuery(id+"F2.imprint","IMPRINT",EDGE,{"derivedFrom":sQuery(id+"F2.wireOp",EDGE,"E30.6.12.0")}),1.0]])]});
            var Q37;
            Q37=makeQuery(id+"F2.imprint","IMPRINT",FACE,{"disambiguationData":[TD([[makeQuery(id+"F2.imprint","IMPRINT",EDGE,{"derivedFrom":sQuery(id+"F2.wireOp",EDGE,"E30.5.10.0")}),1.0]])]});
            var Q38;
            Q38=makeQuery(id+"F2.imprint","IMPRINT",FACE,{"disambiguationData":[TD([[makeQuery(id+"F2.imprint","IMPRINT",EDGE,{"derivedFrom":sQuery(id+"F2.wireOp",EDGE,"E30.4.8.0")}),1.0]])]});
            var Q39;
            Q39=makeQuery(id+"F2.imprint","IMPRINT",FACE,{"disambiguationData":[TD([[makeQuery(id+"F2.imprint","IMPRINT",EDGE,{"derivedFrom":sQuery(id+"F2.wireOp",EDGE,"E30.3.6.0")}),1.0]])]});
            var Q40;
            Q40=makeQuery(id+"F2.imprint","IMPRINT",FACE,{"disambiguationData":[TD([[makeQuery(id+"F2.imprint","IMPRINT",EDGE,{"derivedFrom":sQuery(id+"F2.wireOp",EDGE,"E30.11.6.0")}),1.0]])]});
            var Q41;
            Q41=makeQuery(id+"F2.imprint","IMPRINT",FACE,{"disambiguationData":[TD([[makeQuery(id+"F2.imprint","IMPRINT",EDGE,{"derivedFrom":sQuery(id+"F2.wireOp",EDGE,"E30.10.4.0")}),1.0]])]});
            var Q42;
            Q42=makeQuery(id+"F2.imprint","IMPRINT",FACE,{"disambiguationData":[TD([[makeQuery(id+"F2.imprint","IMPRINT",EDGE,{"derivedFrom":sQuery(id+"F2.wireOp",EDGE,"E30.9.2.0")}),1.0]])]});
            var Q43;
            Q43=makeQuery(id+"F2.imprint","IMPRINT",FACE,{"disambiguationData":[TD([[makeQuery(id+"F2.imprint","IMPRINT",EDGE,{"derivedFrom":sQuery(id+"F2.wireOp",EDGE,"E30.8.0.0")}),1.0]])]});
            var Q44;
            Q44=makeQuery(id+"F2.imprint","IMPRINT",FACE,{"disambiguationData":[TD([[makeQuery(id+"F2.imprint","IMPRINT",EDGE,{"derivedFrom":sQuery(id+"F2.wireOp",EDGE,"E30.13.10.0")}),1.0]])]});
            var Q45;
            Q45=makeQuery(id+"F2.imprint","IMPRINT",FACE,{"disambiguationData":[TD([[makeQuery(id+"F2.imprint","IMPRINT",EDGE,{"derivedFrom":sQuery(id+"F2.wireOp",EDGE,"E30.12.8.0")}),1.0]])]});
            var Q46;
            Q46=makeQuery(id+"F2.imprint","IMPRINT",FACE,{"disambiguationData":[TD([[makeQuery(id+"F2.imprint","IMPRINT",EDGE,{"derivedFrom":sQuery(id+"F2.wireOp",EDGE,"E30.2.5.0")}),1.0]])]});
            var Q47;
            Q47=makeQuery(id+"F2.imprint","IMPRINT",FACE,{"disambiguationData":[TD([[makeQuery(id+"F2.imprint","IMPRINT",EDGE,{"derivedFrom":sQuery(id+"F2.wireOp",EDGE,"E30.1.3.0")}),1.0]])]});
            var Q48;
            Q48=makeQuery(id+"F2.imprint","IMPRINT",FACE,{"disambiguationData":[TD([[makeQuery(id+"F2.imprint","IMPRINT",EDGE,{"derivedFrom":sQuery(id+"F2.wireOp",EDGE,"E30.6.13.0")}),1.0]])]});
            var Q49;
            Q49=makeQuery(id+"F2.imprint","IMPRINT",FACE,{"disambiguationData":[TD([[makeQuery(id+"F2.imprint","IMPRINT",EDGE,{"derivedFrom":sQuery(id+"F2.wireOp",EDGE,"E30.5.11.0")}),1.0]])]});
            var Q50;
            Q50=makeQuery(id+"F2.imprint","IMPRINT",FACE,{"disambiguationData":[TD([[makeQuery(id+"F2.imprint","IMPRINT",EDGE,{"derivedFrom":sQuery(id+"F2.wireOp",EDGE,"E30.4.9.0")}),1.0]])]});
            var Q51;
            Q51=makeQuery(id+"F2.imprint","IMPRINT",FACE,{"disambiguationData":[TD([[makeQuery(id+"F2.imprint","IMPRINT",EDGE,{"derivedFrom":sQuery(id+"F2.wireOp",EDGE,"E30.3.7.0")}),1.0]])]});
            var Q52;
            Q52=makeQuery(id+"F2.imprint","IMPRINT",FACE,{"disambiguationData":[TD([[makeQuery(id+"F2.imprint","IMPRINT",EDGE,{"derivedFrom":sQuery(id+"F2.wireOp",EDGE,"E30.11.7.0")}),1.0]])]});
            var Q53;
            Q53=makeQuery(id+"F2.imprint","IMPRINT",FACE,{"disambiguationData":[TD([[makeQuery(id+"F2.imprint","IMPRINT",EDGE,{"derivedFrom":sQuery(id+"F2.wireOp",EDGE,"E30.10.5.0")}),1.0]])]});
            var Q54;
            Q54=makeQuery(id+"F2.imprint","IMPRINT",FACE,{"disambiguationData":[TD([[makeQuery(id+"F2.imprint","IMPRINT",EDGE,{"derivedFrom":sQuery(id+"F2.wireOp",EDGE,"E30.9.3.0")}),1.0]])]});
            var Q55;
            Q55=makeQuery(id+"F2.imprint","IMPRINT",FACE,{"disambiguationData":[TD([[makeQuery(id+"F2.imprint","IMPRINT",EDGE,{"derivedFrom":sQuery(id+"F2.wireOp",EDGE,"E30.8.1.0")}),1.0]])]});
            var Q56;
            Q56=makeQuery(id+"F2.imprint","IMPRINT",FACE,{"disambiguationData":[TD([[makeQuery(id+"F2.imprint","IMPRINT",EDGE,{"derivedFrom":sQuery(id+"F2.wireOp",EDGE,"E30.13.11.0")}),1.0]])]});
            var Q57;
            Q57=makeQuery(id+"F2.imprint","IMPRINT",FACE,{"disambiguationData":[TD([[makeQuery(id+"F2.imprint","IMPRINT",EDGE,{"derivedFrom":sQuery(id+"F2.wireOp",EDGE,"E30.12.9.0")}),1.0]])]});
            var Q58;
            Q58=makeQuery(id+"F2.imprint","IMPRINT",FACE,{"disambiguationData":[TD([[makeQuery(id+"F2.imprint","IMPRINT",EDGE,{"derivedFrom":sQuery(id+"F2.wireOp",EDGE,"E30.2.6.0")}),1.0]])]});
            var Q59;
            Q59=makeQuery(id+"F2.imprint","IMPRINT",FACE,{"disambiguationData":[TD([[makeQuery(id+"F2.imprint","IMPRINT",EDGE,{"derivedFrom":sQuery(id+"F2.wireOp",EDGE,"E30.1.4.0")}),1.0]])]});
            var Q60;
            Q60=makeQuery(id+"F2.imprint","IMPRINT",FACE,{"disambiguationData":[TD([[makeQuery(id+"F2.imprint","IMPRINT",EDGE,{"derivedFrom":sQuery(id+"F2.wireOp",EDGE,"E30.7.0.0")}),1.0]])]});
            var Q61;
            Q61=makeQuery(id+"F2.imprint","IMPRINT",FACE,{"disambiguationData":[TD([[makeQuery(id+"F2.imprint","IMPRINT",EDGE,{"derivedFrom":sQuery(id+"F2.wireOp",EDGE,"E30.5.12.0")}),1.0]])]});
            var Q62;
            Q62=makeQuery(id+"F2.imprint","IMPRINT",FACE,{"disambiguationData":[TD([[makeQuery(id+"F2.imprint","IMPRINT",EDGE,{"derivedFrom":sQuery(id+"F2.wireOp",EDGE,"E30.4.10.0")}),1.0]])]});
            var Q63;
            Q63=makeQuery(id+"F2.imprint","IMPRINT",FACE,{"disambiguationData":[TD([[makeQuery(id+"F2.imprint","IMPRINT",EDGE,{"derivedFrom":sQuery(id+"F2.wireOp",EDGE,"E30.3.8.0")}),1.0]])]});
            var Q64;
            Q64=makeQuery(id+"F2.imprint","IMPRINT",FACE,{"disambiguationData":[TD([[makeQuery(id+"F2.imprint","IMPRINT",EDGE,{"derivedFrom":sQuery(id+"F2.wireOp",EDGE,"E30.11.8.0")}),1.0]])]});
            var Q65;
            Q65=makeQuery(id+"F2.imprint","IMPRINT",FACE,{"disambiguationData":[TD([[makeQuery(id+"F2.imprint","IMPRINT",EDGE,{"derivedFrom":sQuery(id+"F2.wireOp",EDGE,"E30.10.6.0")}),1.0]])]});
            var Q66;
            Q66=makeQuery(id+"F2.imprint","IMPRINT",FACE,{"disambiguationData":[TD([[makeQuery(id+"F2.imprint","IMPRINT",EDGE,{"derivedFrom":sQuery(id+"F2.wireOp",EDGE,"E30.9.4.0")}),1.0]])]});
            var Q67;
            Q67=makeQuery(id+"F2.imprint","IMPRINT",FACE,{"disambiguationData":[TD([[makeQuery(id+"F2.imprint","IMPRINT",EDGE,{"derivedFrom":sQuery(id+"F2.wireOp",EDGE,"E30.8.2.0")}),1.0]])]});
            var Q68;
            Q68=makeQuery(id+"F2.imprint","IMPRINT",FACE,{"disambiguationData":[TD([[makeQuery(id+"F2.imprint","IMPRINT",EDGE,{"derivedFrom":sQuery(id+"F2.wireOp",EDGE,"E30.13.12.0")}),1.0]])]});
            var Q69;
            Q69=makeQuery(id+"F2.imprint","IMPRINT",FACE,{"disambiguationData":[TD([[makeQuery(id+"F2.imprint","IMPRINT",EDGE,{"derivedFrom":sQuery(id+"F2.wireOp",EDGE,"E30.12.10.0")}),1.0]])]});
            var Q70;
            Q70=makeQuery(id+"F2.imprint","IMPRINT",FACE,{"disambiguationData":[TD([[makeQuery(id+"F2.imprint","IMPRINT",EDGE,{"derivedFrom":sQuery(id+"F2.wireOp",EDGE,"E30.2.7.0")}),1.0]])]});
            var Q71;
            Q71=makeQuery(id+"F2.imprint","IMPRINT",FACE,{"disambiguationData":[TD([[makeQuery(id+"F2.imprint","IMPRINT",EDGE,{"derivedFrom":sQuery(id+"F2.wireOp",EDGE,"E30.7.1.0")}),1.0]])]});
            var Q72;
            Q72=makeQuery(id+"F2.imprint","IMPRINT",FACE,{"disambiguationData":[TD([[makeQuery(id+"F2.imprint","IMPRINT",EDGE,{"derivedFrom":sQuery(id+"F2.wireOp",EDGE,"E30.5.13.0")}),1.0]])]});
            var Q73;
            Q73=makeQuery(id+"F2.imprint","IMPRINT",FACE,{"disambiguationData":[TD([[makeQuery(id+"F2.imprint","IMPRINT",EDGE,{"derivedFrom":sQuery(id+"F2.wireOp",EDGE,"E30.4.11.0")}),1.0]])]});
            var Q74;
            Q74=makeQuery(id+"F2.imprint","IMPRINT",FACE,{"disambiguationData":[TD([[makeQuery(id+"F2.imprint","IMPRINT",EDGE,{"derivedFrom":sQuery(id+"F2.wireOp",EDGE,"E30.3.9.0")}),1.0]])]});
            var Q75;
            Q75=makeQuery(id+"F2.imprint","IMPRINT",FACE,{"disambiguationData":[TD([[makeQuery(id+"F2.imprint","IMPRINT",EDGE,{"derivedFrom":sQuery(id+"F2.wireOp",EDGE,"E30.11.9.0")}),1.0]])]});
            var Q76;
            Q76=makeQuery(id+"F2.imprint","IMPRINT",FACE,{"disambiguationData":[TD([[makeQuery(id+"F2.imprint","IMPRINT",EDGE,{"derivedFrom":sQuery(id+"F2.wireOp",EDGE,"E30.10.7.0")}),1.0]])]});
            var Q77;
            Q77=makeQuery(id+"F2.imprint","IMPRINT",FACE,{"disambiguationData":[TD([[makeQuery(id+"F2.imprint","IMPRINT",EDGE,{"derivedFrom":sQuery(id+"F2.wireOp",EDGE,"E30.9.5.0")}),1.0]])]});
            var Q78;
            Q78=makeQuery(id+"F2.imprint","IMPRINT",FACE,{"disambiguationData":[TD([[makeQuery(id+"F2.imprint","IMPRINT",EDGE,{"derivedFrom":sQuery(id+"F2.wireOp",EDGE,"E30.8.3.0")}),1.0]])]});
            var Q79;
            Q79=makeQuery(id+"F2.imprint","IMPRINT",FACE,{"disambiguationData":[TD([[makeQuery(id+"F2.imprint","IMPRINT",EDGE,{"derivedFrom":sQuery(id+"F2.wireOp",EDGE,"E30.13.13.0")}),1.0]])]});
            var Q80;
            Q80=makeQuery(id+"F2.imprint","IMPRINT",FACE,{"disambiguationData":[TD([[makeQuery(id+"F2.imprint","IMPRINT",EDGE,{"derivedFrom":sQuery(id+"F2.wireOp",EDGE,"E30.12.11.0")}),1.0]])]});
            var Q81;
            Q81=makeQuery(id+"F2.imprint","IMPRINT",FACE,{"disambiguationData":[TD([[makeQuery(id+"F2.imprint","IMPRINT",EDGE,{"derivedFrom":sQuery(id+"F2.wireOp",EDGE,"E30.2.8.0")}),1.0]])]});
            var Q82;
            Q82=makeQuery(id+"F2.imprint","IMPRINT",FACE,{"disambiguationData":[TD([[makeQuery(id+"F2.imprint","IMPRINT",EDGE,{"derivedFrom":sQuery(id+"F2.wireOp",EDGE,"E30.1.6.0")}),1.0]])]});
            var Q83;
            Q83=makeQuery(id+"F2.imprint","IMPRINT",FACE,{"disambiguationData":[TD([[makeQuery(id+"F2.imprint","IMPRINT",EDGE,{"derivedFrom":sQuery(id+"F2.wireOp",EDGE,"E30.7.2.0")}),1.0]])]});
            var Q84;
            Q84=makeQuery(id+"F2.imprint","IMPRINT",FACE,{"disambiguationData":[TD([[makeQuery(id+"F2.imprint","IMPRINT",EDGE,{"derivedFrom":sQuery(id+"F2.wireOp",EDGE,"E30.6.0.0")}),1.0]])]});
            var Q85;
            Q85=makeQuery(id+"F2.imprint","IMPRINT",FACE,{"disambiguationData":[TD([[makeQuery(id+"F2.imprint","IMPRINT",EDGE,{"derivedFrom":sQuery(id+"F2.wireOp",EDGE,"E30.4.12.0")}),1.0]])]});
            var Q86;
            Q86=makeQuery(id+"F2.imprint","IMPRINT",FACE,{"disambiguationData":[TD([[makeQuery(id+"F2.imprint","IMPRINT",EDGE,{"derivedFrom":sQuery(id+"F2.wireOp",EDGE,"E30.3.10.0")}),1.0]])]});
            var Q87;
            Q87=makeQuery(id+"F2.imprint","IMPRINT",FACE,{"disambiguationData":[TD([[makeQuery(id+"F2.imprint","IMPRINT",EDGE,{"derivedFrom":sQuery(id+"F2.wireOp",EDGE,"E30.11.10.0")}),1.0]])]});
            var Q88;
            Q88=makeQuery(id+"F2.imprint","IMPRINT",FACE,{"disambiguationData":[TD([[makeQuery(id+"F2.imprint","IMPRINT",EDGE,{"derivedFrom":sQuery(id+"F2.wireOp",EDGE,"E30.10.8.0")}),1.0]])]});
            var Q89;
            Q89=makeQuery(id+"F2.imprint","IMPRINT",FACE,{"disambiguationData":[TD([[makeQuery(id+"F2.imprint","IMPRINT",EDGE,{"derivedFrom":sQuery(id+"F2.wireOp",EDGE,"E30.9.6.0")}),1.0]])]});
            var Q90;
            Q90=makeQuery(id+"F2.imprint","IMPRINT",FACE,{"disambiguationData":[TD([[makeQuery(id+"F2.imprint","IMPRINT",EDGE,{"derivedFrom":sQuery(id+"F2.wireOp",EDGE,"E30.8.4.0")}),1.0]])]});
            var Q91;
            Q91=makeQuery(id+"F2.imprint","IMPRINT",FACE,{"disambiguationData":[TD([[makeQuery(id+"F2.imprint","IMPRINT",EDGE,{"derivedFrom":sQuery(id+"F2.wireOp",EDGE,"E30.12.12.0")}),1.0]])]});
            var Q92;
            Q92=makeQuery(id+"F2.imprint","IMPRINT",FACE,{"disambiguationData":[TD([[makeQuery(id+"F2.imprint","IMPRINT",EDGE,{"derivedFrom":sQuery(id+"F2.wireOp",EDGE,"E30.2.9.0")}),1.0]])]});
            var Q93;
            Q93=makeQuery(id+"F2.imprint","IMPRINT",FACE,{"disambiguationData":[TD([[makeQuery(id+"F2.imprint","IMPRINT",EDGE,{"derivedFrom":sQuery(id+"F2.wireOp",EDGE,"E30.1.7.0")}),1.0]])]});
            var Q94;
            Q94=makeQuery(id+"F2.imprint","IMPRINT",FACE,{"disambiguationData":[TD([[makeQuery(id+"F2.imprint","IMPRINT",EDGE,{"derivedFrom":sQuery(id+"F2.wireOp",EDGE,"E30.7.3.0")}),1.0]])]});
            var Q95;
            Q95=makeQuery(id+"F2.imprint","IMPRINT",FACE,{"disambiguationData":[TD([[makeQuery(id+"F2.imprint","IMPRINT",EDGE,{"derivedFrom":sQuery(id+"F2.wireOp",EDGE,"E30.6.1.0")}),1.0]])]});
            var Q96;
            Q96=makeQuery(id+"F2.imprint","IMPRINT",FACE,{"disambiguationData":[TD([[makeQuery(id+"F2.imprint","IMPRINT",EDGE,{"derivedFrom":sQuery(id+"F2.wireOp",EDGE,"E30.4.13.0")}),1.0]])]});
            var Q97;
            Q97=makeQuery(id+"F2.imprint","IMPRINT",FACE,{"disambiguationData":[TD([[makeQuery(id+"F2.imprint","IMPRINT",EDGE,{"derivedFrom":sQuery(id+"F2.wireOp",EDGE,"E30.3.11.0")}),1.0]])]});
            var Q98;
            Q98=makeQuery(id+"F2.imprint","IMPRINT",FACE,{"disambiguationData":[TD([[makeQuery(id+"F2.imprint","IMPRINT",EDGE,{"derivedFrom":sQuery(id+"F2.wireOp",EDGE,"E30.11.11.0")}),1.0]])]});
            var Q99;
            Q99=makeQuery(id+"F2.imprint","IMPRINT",FACE,{"disambiguationData":[TD([[makeQuery(id+"F2.imprint","IMPRINT",EDGE,{"derivedFrom":sQuery(id+"F2.wireOp",EDGE,"E30.10.9.0")}),1.0]])]});
            var Q100;
            Q100=makeQuery(id+"F2.imprint","IMPRINT",FACE,{"disambiguationData":[TD([[makeQuery(id+"F2.imprint","IMPRINT",EDGE,{"derivedFrom":sQuery(id+"F2.wireOp",EDGE,"E30.9.7.0")}),1.0]])]});
            var Q101;
            Q101=makeQuery(id+"F2.imprint","IMPRINT",FACE,{"disambiguationData":[TD([[makeQuery(id+"F2.imprint","IMPRINT",EDGE,{"derivedFrom":sQuery(id+"F2.wireOp",EDGE,"E30.8.5.0")}),1.0]])]});
            var Q102;
            Q102=makeQuery(id+"F2.imprint","IMPRINT",FACE,{"disambiguationData":[TD([[makeQuery(id+"F2.imprint","IMPRINT",EDGE,{"derivedFrom":sQuery(id+"F2.wireOp",EDGE,"E30.12.13.0")}),1.0]])]});
            var Q103;
            Q103=makeQuery(id+"F2.imprint","IMPRINT",FACE,{"disambiguationData":[TD([[makeQuery(id+"F2.imprint","IMPRINT",EDGE,{"derivedFrom":sQuery(id+"F2.wireOp",EDGE,"E30.5.0.0")}),1.0]])]});
            var Q104;
            Q104=makeQuery(id+"F2.imprint","IMPRINT",FACE,{"disambiguationData":[TD([[makeQuery(id+"F2.imprint","IMPRINT",EDGE,{"derivedFrom":sQuery(id+"F2.wireOp",EDGE,"E30.3.12.0")}),1.0]])]});
            var Q105;
            Q105=makeQuery(id+"F2.imprint","IMPRINT",FACE,{"disambiguationData":[TD([[makeQuery(id+"F2.imprint","IMPRINT",EDGE,{"derivedFrom":sQuery(id+"F2.wireOp",EDGE,"E30.2.10.0")}),1.0]])]});
            var Q106;
            Q106=makeQuery(id+"F2.imprint","IMPRINT",FACE,{"disambiguationData":[TD([[makeQuery(id+"F2.imprint","IMPRINT",EDGE,{"derivedFrom":sQuery(id+"F2.wireOp",EDGE,"E30.1.8.0")}),1.0]])]});
            var Q107;
            Q107=makeQuery(id+"F2.imprint","IMPRINT",FACE,{"disambiguationData":[TD([[makeQuery(id+"F2.imprint","IMPRINT",EDGE,{"derivedFrom":sQuery(id+"F2.wireOp",EDGE,"E30.9.8.0")}),1.0]])]});
            var Q108;
            Q108=makeQuery(id+"F2.imprint","IMPRINT",FACE,{"disambiguationData":[TD([[makeQuery(id+"F2.imprint","IMPRINT",EDGE,{"derivedFrom":sQuery(id+"F2.wireOp",EDGE,"E30.8.6.0")}),1.0]])]});
            var Q109;
            Q109=makeQuery(id+"F2.imprint","IMPRINT",FACE,{"disambiguationData":[TD([[makeQuery(id+"F2.imprint","IMPRINT",EDGE,{"derivedFrom":sQuery(id+"F2.wireOp",EDGE,"E30.7.4.0")}),1.0]])]});
            var Q110;
            Q110=makeQuery(id+"F2.imprint","IMPRINT",FACE,{"disambiguationData":[TD([[makeQuery(id+"F2.imprint","IMPRINT",EDGE,{"derivedFrom":sQuery(id+"F2.wireOp",EDGE,"E30.6.2.0")}),1.0]])]});
            var Q111;
            Q111=makeQuery(id+"F2.imprint","IMPRINT",FACE,{"disambiguationData":[TD([[makeQuery(id+"F2.imprint","IMPRINT",EDGE,{"derivedFrom":sQuery(id+"F2.wireOp",EDGE,"E30.13.0.0")}),1.0]])]});
            var Q112;
            Q112=makeQuery(id+"F2.imprint","IMPRINT",FACE,{"disambiguationData":[TD([[makeQuery(id+"F2.imprint","IMPRINT",EDGE,{"derivedFrom":sQuery(id+"F2.wireOp",EDGE,"E30.11.12.0")}),1.0]])]});
            var Q113;
            Q113=makeQuery(id+"F2.imprint","IMPRINT",FACE,{"disambiguationData":[TD([[makeQuery(id+"F2.imprint","IMPRINT",EDGE,{"derivedFrom":sQuery(id+"F2.wireOp",EDGE,"E30.10.10.0")}),1.0]])]});
            var Q114;
            Q114=makeQuery(id+"F2.imprint","IMPRINT",FACE,{"disambiguationData":[TD([[makeQuery(id+"F2.imprint","IMPRINT",EDGE,{"derivedFrom":sQuery(id+"F2.wireOp",EDGE,"E30.9.9.0")}),1.0]])]});
            var Q115;
            Q115=makeQuery(id+"F2.imprint","IMPRINT",FACE,{"disambiguationData":[TD([[makeQuery(id+"F2.imprint","IMPRINT",EDGE,{"derivedFrom":sQuery(id+"F2.wireOp",EDGE,"E30.8.7.0")}),1.0]])]});
            var Q116;
            Q116=makeQuery(id+"F2.imprint","IMPRINT",FACE,{"disambiguationData":[TD([[makeQuery(id+"F2.imprint","IMPRINT",EDGE,{"derivedFrom":sQuery(id+"F2.wireOp",EDGE,"E30.7.5.0")}),1.0]])]});
            var Q117;
            Q117=makeQuery(id+"F2.imprint","IMPRINT",FACE,{"disambiguationData":[TD([[makeQuery(id+"F2.imprint","IMPRINT",EDGE,{"derivedFrom":sQuery(id+"F2.wireOp",EDGE,"E30.6.3.0")}),1.0]])]});
            var Q118;
            Q118=makeQuery(id+"F2.imprint","IMPRINT",FACE,{"disambiguationData":[TD([[makeQuery(id+"F2.imprint","IMPRINT",EDGE,{"derivedFrom":sQuery(id+"F2.wireOp",EDGE,"E30.13.1.0")}),1.0]])]});
            var Q119;
            Q119=makeQuery(id+"F2.imprint","IMPRINT",FACE,{"disambiguationData":[TD([[makeQuery(id+"F2.imprint","IMPRINT",EDGE,{"derivedFrom":sQuery(id+"F2.wireOp",EDGE,"E30.11.13.0")}),1.0]])]});
            var Q120;
            Q120=makeQuery(id+"F2.imprint","IMPRINT",FACE,{"disambiguationData":[TD([[makeQuery(id+"F2.imprint","IMPRINT",EDGE,{"derivedFrom":sQuery(id+"F2.wireOp",EDGE,"E30.10.11.0")}),1.0]])]});
            var Q121;
            Q121=makeQuery(id+"F2.imprint","IMPRINT",FACE,{"disambiguationData":[TD([[makeQuery(id+"F2.imprint","IMPRINT",EDGE,{"derivedFrom":sQuery(id+"F2.wireOp",EDGE,"E30.5.1.0")}),1.0]])]});
            var Q122;
            Q122=makeQuery(id+"F2.imprint","IMPRINT",FACE,{"disambiguationData":[TD([[makeQuery(id+"F2.imprint","IMPRINT",EDGE,{"derivedFrom":sQuery(id+"F2.wireOp",EDGE,"E30.3.13.0")}),1.0]])]});
            var Q123;
            Q123=makeQuery(id+"F2.imprint","IMPRINT",FACE,{"disambiguationData":[TD([[makeQuery(id+"F2.imprint","IMPRINT",EDGE,{"derivedFrom":sQuery(id+"F2.wireOp",EDGE,"E30.2.11.0")}),1.0]])]});
            var Q124;
            Q124=makeQuery(id+"F2.imprint","IMPRINT",FACE,{"disambiguationData":[TD([[makeQuery(id+"F2.imprint","IMPRINT",EDGE,{"derivedFrom":sQuery(id+"F2.wireOp",EDGE,"E30.1.9.0")}),1.0]])]});
            var Q125;
            Q125=makeQuery(id+"F2.imprint","IMPRINT",FACE,{"disambiguationData":[TD([[makeQuery(id+"F2.imprint","IMPRINT",EDGE,{"derivedFrom":sQuery(id+"F2.wireOp",EDGE,"E30.13.2.0")}),1.0]])]});
            var Q126;
            Q126=makeQuery(id+"F2.imprint","IMPRINT",FACE,{"disambiguationData":[TD([[makeQuery(id+"F2.imprint","IMPRINT",EDGE,{"derivedFrom":sQuery(id+"F2.wireOp",EDGE,"E30.12.0.0")}),1.0]])]});
            var Q127;
            Q127=makeQuery(id+"F2.imprint","IMPRINT",FACE,{"disambiguationData":[TD([[makeQuery(id+"F2.imprint","IMPRINT",EDGE,{"derivedFrom":sQuery(id+"F2.wireOp",EDGE,"E30.10.12.0")}),1.0]])]});
            var Q128;
            Q128=makeQuery(id+"F2.imprint","IMPRINT",FACE,{"disambiguationData":[TD([[makeQuery(id+"F2.imprint","IMPRINT",EDGE,{"derivedFrom":sQuery(id+"F2.wireOp",EDGE,"E30.5.2.0")}),1.0]])]});
            var Q129;
            Q129=makeQuery(id+"F2.imprint","IMPRINT",FACE,{"disambiguationData":[TD([[makeQuery(id+"F2.imprint","IMPRINT",EDGE,{"derivedFrom":sQuery(id+"F2.wireOp",EDGE,"E30.4.0.0")}),1.0]])]});
            var Q130;
            Q130=makeQuery(id+"F2.imprint","IMPRINT",FACE,{"disambiguationData":[TD([[makeQuery(id+"F2.imprint","IMPRINT",EDGE,{"derivedFrom":sQuery(id+"F2.wireOp",EDGE,"E30.2.12.0")}),1.0]])]});
            var Q131;
            Q131=makeQuery(id+"F2.imprint","IMPRINT",FACE,{"disambiguationData":[TD([[makeQuery(id+"F2.imprint","IMPRINT",EDGE,{"derivedFrom":sQuery(id+"F2.wireOp",EDGE,"E30.1.10.0")}),1.0]])]});
            var Q132;
            Q132=makeQuery(id+"F2.imprint","IMPRINT",FACE,{"disambiguationData":[TD([[makeQuery(id+"F2.imprint","IMPRINT",EDGE,{"derivedFrom":sQuery(id+"F2.wireOp",EDGE,"E30.9.10.0")}),1.0]])]});
            var Q133;
            Q133=makeQuery(id+"F2.imprint","IMPRINT",FACE,{"disambiguationData":[TD([[makeQuery(id+"F2.imprint","IMPRINT",EDGE,{"derivedFrom":sQuery(id+"F2.wireOp",EDGE,"E30.8.8.0")}),1.0]])]});
            var Q134;
            Q134=makeQuery(id+"F2.imprint","IMPRINT",FACE,{"disambiguationData":[TD([[makeQuery(id+"F2.imprint","IMPRINT",EDGE,{"derivedFrom":sQuery(id+"F2.wireOp",EDGE,"E30.7.6.0")}),1.0]])]});
            var Q135;
            Q135=makeQuery(id+"F2.imprint","IMPRINT",FACE,{"disambiguationData":[TD([[makeQuery(id+"F2.imprint","IMPRINT",EDGE,{"derivedFrom":sQuery(id+"F2.wireOp",EDGE,"E30.6.4.0")}),1.0]])]});
            var Q136;
            Q136=makeQuery(id+"F2.imprint","IMPRINT",FACE,{"disambiguationData":[TD([[makeQuery(id+"F2.imprint","IMPRINT",EDGE,{"derivedFrom":sQuery(id+"F2.wireOp",EDGE,"E30.5.3.0")}),1.0]])]});
            var Q137;
            Q137=makeQuery(id+"F2.imprint","IMPRINT",FACE,{"disambiguationData":[TD([[makeQuery(id+"F2.imprint","IMPRINT",EDGE,{"derivedFrom":sQuery(id+"F2.wireOp",EDGE,"E30.4.1.0")}),1.0]])]});
            var Q138;
            Q138=makeQuery(id+"F2.imprint","IMPRINT",FACE,{"disambiguationData":[TD([[makeQuery(id+"F2.imprint","IMPRINT",EDGE,{"derivedFrom":sQuery(id+"F2.wireOp",EDGE,"E30.2.13.0")}),1.0]])]});
            var Q139;
            Q139=makeQuery(id+"F2.imprint","IMPRINT",FACE,{"disambiguationData":[TD([[makeQuery(id+"F2.imprint","IMPRINT",EDGE,{"derivedFrom":sQuery(id+"F2.wireOp",EDGE,"E30.1.11.0")}),1.0]])]});
            var Q140;
            Q140=makeQuery(id+"F2.imprint","IMPRINT",FACE,{"disambiguationData":[TD([[makeQuery(id+"F2.imprint","IMPRINT",EDGE,{"derivedFrom":sQuery(id+"F2.wireOp",EDGE,"E30.9.11.0")}),1.0]])]});
            var Q141;
            Q141=makeQuery(id+"F2.imprint","IMPRINT",FACE,{"disambiguationData":[TD([[makeQuery(id+"F2.imprint","IMPRINT",EDGE,{"derivedFrom":sQuery(id+"F2.wireOp",EDGE,"E30.8.9.0")}),1.0]])]});
            var Q142;
            Q142=makeQuery(id+"F2.imprint","IMPRINT",FACE,{"disambiguationData":[TD([[makeQuery(id+"F2.imprint","IMPRINT",EDGE,{"derivedFrom":sQuery(id+"F2.wireOp",EDGE,"E30.7.7.0")}),1.0]])]});
            var Q143;
            Q143=makeQuery(id+"F2.imprint","IMPRINT",FACE,{"disambiguationData":[TD([[makeQuery(id+"F2.imprint","IMPRINT",EDGE,{"derivedFrom":sQuery(id+"F2.wireOp",EDGE,"E30.6.5.0")}),1.0]])]});
            var Q144;
            Q144=makeQuery(id+"F2.imprint","IMPRINT",FACE,{"disambiguationData":[TD([[makeQuery(id+"F2.imprint","IMPRINT",EDGE,{"derivedFrom":sQuery(id+"F2.wireOp",EDGE,"E30.13.3.0")}),1.0]])]});
            var Q145;
            Q145=makeQuery(id+"F2.imprint","IMPRINT",FACE,{"disambiguationData":[TD([[makeQuery(id+"F2.imprint","IMPRINT",EDGE,{"derivedFrom":sQuery(id+"F2.wireOp",EDGE,"E30.12.1.0")}),1.0]])]});
            var Q146;
            Q146=makeQuery(id+"F2.imprint","IMPRINT",FACE,{"disambiguationData":[TD([[makeQuery(id+"F2.imprint","IMPRINT",EDGE,{"derivedFrom":sQuery(id+"F2.wireOp",EDGE,"E30.10.13.0")}),1.0]])]});
            var Q147;
            Q147=makeQuery(id+"F2.imprint","IMPRINT",FACE,{"disambiguationData":[TD([[makeQuery(id+"F2.imprint","IMPRINT",EDGE,{"derivedFrom":sQuery(id+"F2.wireOp",EDGE,"E30.5.4.0")}),1.0]])]});
            var Q148;
            Q148=makeQuery(id+"F2.imprint","IMPRINT",FACE,{"disambiguationData":[TD([[makeQuery(id+"F2.imprint","IMPRINT",EDGE,{"derivedFrom":sQuery(id+"F2.wireOp",EDGE,"E30.4.2.0")}),1.0]])]});
            var Q149;
            Q149=makeQuery(id+"F2.imprint","IMPRINT",FACE,{"disambiguationData":[TD([[makeQuery(id+"F2.imprint","IMPRINT",EDGE,{"derivedFrom":sQuery(id+"F2.wireOp",EDGE,"E30.3.0.0")}),1.0]])]});
            var Q150;
            Q150=makeQuery(id+"F2.imprint","IMPRINT",FACE,{"disambiguationData":[TD([[makeQuery(id+"F2.imprint","IMPRINT",EDGE,{"derivedFrom":sQuery(id+"F2.wireOp",EDGE,"E30.1.12.0")}),1.0]])]});
            var Q151;
            Q151=makeQuery(id+"F2.imprint","IMPRINT",FACE,{"disambiguationData":[TD([[makeQuery(id+"F2.imprint","IMPRINT",EDGE,{"derivedFrom":sQuery(id+"F2.wireOp",EDGE,"E30.9.12.0")}),1.0]])]});
            var Q152;
            Q152=makeQuery(id+"F2.imprint","IMPRINT",FACE,{"disambiguationData":[TD([[makeQuery(id+"F2.imprint","IMPRINT",EDGE,{"derivedFrom":sQuery(id+"F2.wireOp",EDGE,"E30.8.10.0")}),1.0]])]});
            var Q153;
            Q153=makeQuery(id+"F2.imprint","IMPRINT",FACE,{"disambiguationData":[TD([[makeQuery(id+"F2.imprint","IMPRINT",EDGE,{"derivedFrom":sQuery(id+"F2.wireOp",EDGE,"E30.7.8.0")}),1.0]])]});
            var Q154;
            Q154=makeQuery(id+"F2.imprint","IMPRINT",FACE,{"disambiguationData":[TD([[makeQuery(id+"F2.imprint","IMPRINT",EDGE,{"derivedFrom":sQuery(id+"F2.wireOp",EDGE,"E30.6.6.0")}),1.0]])]});
            var Q155;
            Q155=makeQuery(id+"F2.imprint","IMPRINT",FACE,{"disambiguationData":[TD([[makeQuery(id+"F2.imprint","IMPRINT",EDGE,{"derivedFrom":sQuery(id+"F2.wireOp",EDGE,"E30.13.4.0")}),1.0]])]});
            var Q156;
            Q156=makeQuery(id+"F2.imprint","IMPRINT",FACE,{"disambiguationData":[TD([[makeQuery(id+"F2.imprint","IMPRINT",EDGE,{"derivedFrom":sQuery(id+"F2.wireOp",EDGE,"E30.12.2.0")}),1.0]])]});
            var Q157;
            Q157=makeQuery(id+"F2.imprint","IMPRINT",FACE,{"disambiguationData":[TD([[makeQuery(id+"F2.imprint","IMPRINT",EDGE,{"derivedFrom":sQuery(id+"F2.wireOp",EDGE,"E30.11.0.0")}),1.0]])]});
            var Q158;
            Q158=makeQuery(id+"F2.imprint","IMPRINT",FACE,{"disambiguationData":[TD([[makeQuery(id+"F2.imprint","IMPRINT",EDGE,{"derivedFrom":sQuery(id+"F2.wireOp",EDGE,"E30.5.5.0")}),1.0]])]});
            var Q159;
            Q159=makeQuery(id+"F2.imprint","IMPRINT",FACE,{"disambiguationData":[TD([[makeQuery(id+"F2.imprint","IMPRINT",EDGE,{"derivedFrom":sQuery(id+"F2.wireOp",EDGE,"E30.4.3.0")}),1.0]])]});
            var Q160;
            Q160=makeQuery(id+"F2.imprint","IMPRINT",FACE,{"disambiguationData":[TD([[makeQuery(id+"F2.imprint","IMPRINT",EDGE,{"derivedFrom":sQuery(id+"F2.wireOp",EDGE,"E30.3.1.0")}),1.0]])]});
            var Q161;
            Q161=makeQuery(id+"F2.imprint","IMPRINT",FACE,{"disambiguationData":[TD([[makeQuery(id+"F2.imprint","IMPRINT",EDGE,{"derivedFrom":sQuery(id+"F2.wireOp",EDGE,"E30.1.13.0")}),1.0]])]});
            var Q162;
            Q162=makeQuery(id+"F2.imprint","IMPRINT",FACE,{"disambiguationData":[TD([[makeQuery(id+"F2.imprint","IMPRINT",EDGE,{"derivedFrom":sQuery(id+"F2.wireOp",EDGE,"E30.9.13.0")}),1.0]])]});
            var Q163;
            Q163=makeQuery(id+"F2.imprint","IMPRINT",FACE,{"disambiguationData":[TD([[makeQuery(id+"F2.imprint","IMPRINT",EDGE,{"derivedFrom":sQuery(id+"F2.wireOp",EDGE,"E30.8.11.0")}),1.0]])]});
            var Q164;
            Q164=makeQuery(id+"F2.imprint","IMPRINT",FACE,{"disambiguationData":[TD([[makeQuery(id+"F2.imprint","IMPRINT",EDGE,{"derivedFrom":sQuery(id+"F2.wireOp",EDGE,"E30.7.9.0")}),1.0]])]});
            var Q165;
            Q165=makeQuery(id+"F2.imprint","IMPRINT",FACE,{"disambiguationData":[TD([[makeQuery(id+"F2.imprint","IMPRINT",EDGE,{"derivedFrom":sQuery(id+"F2.wireOp",EDGE,"E30.6.7.0")}),1.0]])]});
            var Q166;
            Q166=makeQuery(id+"F2.imprint","IMPRINT",FACE,{"disambiguationData":[TD([[makeQuery(id+"F2.imprint","IMPRINT",EDGE,{"derivedFrom":sQuery(id+"F2.wireOp",EDGE,"E30.13.5.0")}),1.0]])]});
            var Q167;
            Q167=makeQuery(id+"F2.imprint","IMPRINT",FACE,{"disambiguationData":[TD([[makeQuery(id+"F2.imprint","IMPRINT",EDGE,{"derivedFrom":sQuery(id+"F2.wireOp",EDGE,"E30.12.3.0")}),1.0]])]});
            var Q168;
            Q168=makeQuery(id+"F2.imprint","IMPRINT",FACE,{"disambiguationData":[TD([[makeQuery(id+"F2.imprint","IMPRINT",EDGE,{"derivedFrom":sQuery(id+"F2.wireOp",EDGE,"E30.11.1.0")}),1.0]])]});
            var Q169;
            Q169=makeQuery(id+"F2.imprint","IMPRINT",FACE,{"disambiguationData":[TD([[makeQuery(id+"F2.imprint","IMPRINT",EDGE,{"derivedFrom":sQuery(id+"F2.wireOp",EDGE,"E30.5.6.0")}),1.0]])]});
            var Q170;
            Q170=makeQuery(id+"F2.imprint","IMPRINT",FACE,{"disambiguationData":[TD([[makeQuery(id+"F2.imprint","IMPRINT",EDGE,{"derivedFrom":sQuery(id+"F2.wireOp",EDGE,"E30.4.4.0")}),1.0]])]});
            var Q171;
            Q171=makeQuery(id+"F2.imprint","IMPRINT",FACE,{"disambiguationData":[TD([[makeQuery(id+"F2.imprint","IMPRINT",EDGE,{"derivedFrom":sQuery(id+"F2.wireOp",EDGE,"E30.3.2.0")}),1.0]])]});
            var Q172;
            Q172=makeQuery(id+"F2.imprint","IMPRINT",FACE,{"disambiguationData":[TD([[makeQuery(id+"F2.imprint","IMPRINT",EDGE,{"derivedFrom":sQuery(id+"F2.wireOp",EDGE,"E30.2.0.0")}),1.0]])]});
            var Q173;
            Q173=makeQuery(id+"F2.imprint","IMPRINT",FACE,{"disambiguationData":[TD([[makeQuery(id+"F2.imprint","IMPRINT",EDGE,{"derivedFrom":sQuery(id+"F2.wireOp",EDGE,"E30.10.0.0")}),1.0]])]});
            var Q174;
            Q174=makeQuery(id+"F2.imprint","IMPRINT",FACE,{"disambiguationData":[TD([[makeQuery(id+"F2.imprint","IMPRINT",EDGE,{"derivedFrom":sQuery(id+"F2.wireOp",EDGE,"E30.8.12.0")}),1.0]])]});
            var Q175;
            Q175=makeQuery(id+"F2.imprint","IMPRINT",FACE,{"disambiguationData":[TD([[makeQuery(id+"F2.imprint","IMPRINT",EDGE,{"derivedFrom":sQuery(id+"F2.wireOp",EDGE,"E30.7.10.0")}),1.0]])]});
            var Q176;
            Q176=makeQuery(id+"F2.imprint","IMPRINT",FACE,{"disambiguationData":[TD([[makeQuery(id+"F2.imprint","IMPRINT",EDGE,{"derivedFrom":sQuery(id+"F2.wireOp",EDGE,"E30.6.8.0")}),1.0]])]});
            var Q177;
            Q177=makeQuery(id+"F2.imprint","IMPRINT",FACE,{"disambiguationData":[TD([[makeQuery(id+"F2.imprint","IMPRINT",EDGE,{"derivedFrom":sQuery(id+"F2.wireOp",EDGE,"E30.13.6.0")}),1.0]])]});
            var Q178;
            Q178=makeQuery(id+"F2.imprint","IMPRINT",FACE,{"disambiguationData":[TD([[makeQuery(id+"F2.imprint","IMPRINT",EDGE,{"derivedFrom":sQuery(id+"F2.wireOp",EDGE,"E30.12.4.0")}),1.0]])]});
            var Q179;
            Q179=makeQuery(id+"F2.imprint","IMPRINT",FACE,{"disambiguationData":[TD([[makeQuery(id+"F2.imprint","IMPRINT",EDGE,{"derivedFrom":sQuery(id+"F2.wireOp",EDGE,"E30.11.2.0")}),1.0]])]});
            var Q180;
            Q180=makeQuery(id+"F2.imprint","IMPRINT",FACE,{"disambiguationData":[TD([[makeQuery(id+"F2.imprint","IMPRINT",EDGE,{"derivedFrom":sQuery(id+"F2.wireOp",EDGE,"E30.1.1.0")}),1.0]])]});
            var Q181;
            Q181=makeQuery(id+"F2.imprint","IMPRINT",FACE,{"disambiguationData":[TD([[makeQuery(id+"F2.imprint","IMPRINT",EDGE,{"derivedFrom":sQuery(id+"F2.wireOp",EDGE,"E30.0.13.0")}),1.0]])]});
            var Q182;
            Q182=makeQuery(id+"F2.imprint","IMPRINT",FACE,{"disambiguationData":[TD([[makeQuery(id+"F2.imprint","IMPRINT",EDGE,{"derivedFrom":sQuery(id+"F2.wireOp",EDGE,"E30.0.2.0")}),1.0]])]});
            var Q183;
            Q183=makeQuery(id+"F2.imprint","IMPRINT",FACE,{"disambiguationData":[TD([[makeQuery(id+"F2.imprint","IMPRINT",EDGE,{"derivedFrom":sQuery(id+"F2.wireOp",EDGE,"E30.0.3.0")}),1.0]])]});
            var Q184;
            Q184=makeQuery(id+"F2.imprint","IMPRINT",FACE,{"disambiguationData":[TD([[makeQuery(id+"F2.imprint","IMPRINT",EDGE,{"derivedFrom":sQuery(id+"F2.wireOp",EDGE,"E30.0.4.0")}),1.0]])]});
            var Q185;
            Q185=makeQuery(id+"F2.imprint","IMPRINT",FACE,{"disambiguationData":[TD([[makeQuery(id+"F2.imprint","IMPRINT",EDGE,{"derivedFrom":sQuery(id+"F2.wireOp",EDGE,"E30.0.6.0")}),1.0]])]});
            var Q186;
            Q186=makeQuery(id+"F2.imprint","IMPRINT",FACE,{"disambiguationData":[TD([[makeQuery(id+"F2.imprint","IMPRINT",EDGE,{"derivedFrom":sQuery(id+"F2.wireOp",EDGE,"E30.0.7.0")}),1.0]])]});
            var Q187;
            Q187=makeQuery(id+"F2.imprint","IMPRINT",FACE,{"disambiguationData":[TD([[makeQuery(id+"F2.imprint","IMPRINT",EDGE,{"derivedFrom":sQuery(id+"F2.wireOp",EDGE,"E30.0.8.0")}),1.0]])]});
            var Q188;
            Q188=makeQuery(id+"F2.imprint","IMPRINT",FACE,{"disambiguationData":[TD([[makeQuery(id+"F2.imprint","IMPRINT",EDGE,{"derivedFrom":sQuery(id+"F2.wireOp",EDGE,"E30.0.9.0")}),1.0]])]});
            var Q189;
            Q189=makeQuery(id+"F2.imprint","IMPRINT",FACE,{"disambiguationData":[TD([[makeQuery(id+"F2.imprint","IMPRINT",EDGE,{"derivedFrom":sQuery(id+"F2.wireOp",EDGE,"E30.0.10.0")}),1.0]])]});
            var Q190;
            Q190=makeQuery(id+"F2.imprint","IMPRINT",FACE,{"disambiguationData":[TD([[makeQuery(id+"F2.imprint","IMPRINT",EDGE,{"derivedFrom":sQuery(id+"F2.wireOp",EDGE,"E30.0.11.0")}),1.0]])]});
            var Q191;
            Q191=makeQuery(id+"F2.imprint","IMPRINT",FACE,{"disambiguationData":[TD([[makeQuery(id+"F2.imprint","IMPRINT",EDGE,{"derivedFrom":sQuery(id+"F2.wireOp",EDGE,"E30.0.12.0")}),1.0]])]});
            var Q192;
            Q192=makeQuery(id+"F2.imprint","IMPRINT",FACE,{"disambiguationData":[TD([[makeQuery(id+"F2.imprint","IMPRINT",EDGE,{"derivedFrom":sQuery(id+"F2.wireOp",EDGE,"E30.1.0.0")}),1.0]])]});
            var Q193;
            Q193=makeQuery(id+"F2.imprint","IMPRINT",FACE,{"disambiguationData":[TD([[makeQuery(id+"F2.imprint","IMPRINT",EDGE,{"derivedFrom":sQuery(id+"F2.wireOp",EDGE,"E30.0.1.0")}),1.0]])]});
            var Q194;
            Q194=makeQuery(id+"F2.imprint","IMPRINT",FACE,{"disambiguationData":[TD([[makeQuery(id+"F2.imprint","IMPRINT",EDGE,{"derivedFrom":sQuery(id+"F2.wireOp",EDGE,"E29")}),1.0]])]});
            var Q195;
            Q195=makeQuery(id+"F2.imprint","IMPRINT",FACE,{"disambiguationData":[TD([[makeQuery(id+"F2.imprint","IMPRINT",EDGE,{"derivedFrom":sQuery(id+"F2.wireOp",EDGE,"E30.1.5.0")}),1.0]])]});
            var Q196;
            Q196=sQuery(id+"F2.wireOp",EDGE,"E30.13.13.0");
            var Q197;
            Q197=sQuery(id+"F2.wireOp",EDGE,"E30.13.0.0");
            var Q198;
            Q198=sQuery(id+"F2.wireOp",EDGE,"E30.13.1.0");
            var Q199;
            Q199=sQuery(id+"F2.wireOp",EDGE,"E30.13.11.0");
            var Q200;
            Q200=sQuery(id+"F2.wireOp",EDGE,"E30.13.12.0");
            var Q201;
            Q201=sQuery(id+"F2.wireOp",EDGE,"E30.0.13.0");
            var Q202;
            Q202=sQuery(id+"F2.wireOp",EDGE,"E30.13.8.0");
            var Q203;
            Q203=sQuery(id+"F2.wireOp",EDGE,"E30.9.0.0");
            var Q204;
            Q204=sQuery(id+"F2.wireOp",EDGE,"E30.11.5.0");
            var Q205;
            Q205=sQuery(id+"F2.wireOp",EDGE,"E30.13.9.0");
            var Q206;
            Q206=sQuery(id+"F2.wireOp",EDGE,"E30.10.4.0");
            var Q207;
            Q207=sQuery(id+"F2.wireOp",EDGE,"E30.13.10.0");
            var Q208;
            Q208=sQuery(id+"F2.wireOp",EDGE,"E30.13.3.0");
            var Q209;
            Q209=sQuery(id+"F2.wireOp",EDGE,"E30.13.4.0");
            var Q210;
            Q210=sQuery(id+"F2.wireOp",EDGE,"E30.11.0.0");
            var Q211;
            Q211=sQuery(id+"F2.wireOp",EDGE,"E30.1.13.0");
            var Q212;
            Q212=sQuery(id+"F2.wireOp",EDGE,"E30.13.5.0");
            var Q213;
            Q213=sQuery(id+"F2.wireOp",EDGE,"E30.11.1.0");
            var Q214;
            Q214=sQuery(id+"F2.wireOp",EDGE,"E30.10.0.0");
            var Q215;
            Q215=sQuery(id+"F2.wireOp",EDGE,"E30.13.6.0");
            var Q216;
            Q216=sQuery(id+"F2.wireOp",EDGE,"E30.12.4.0");
            var Q217;
            Q217=sQuery(id+"F2.wireOp",EDGE,"E30.11.2.0");
            var Q218;
            Q218=sQuery(id+"F2.wireOp",EDGE,"E30.0.12.0");
            var Q219;
            Q219=sQuery(id+"F2.wireOp",EDGE,"E30.10.1.0");
            var Q220;
            Q220=sQuery(id+"F2.wireOp",EDGE,"E30.13.7.0");
            var Q221;
            Q221=sQuery(id+"F2.wireOp",EDGE,"E30.12.5.0");
            var Q222;
            Q222=sQuery(id+"F2.wireOp",EDGE,"E30.10.3.0");
            var Q223;
            Q223=sQuery(id+"F2.wireOp",EDGE,"E30.9.1.0");
            var Q224;
            Q224=sQuery(id+"F2.wireOp",EDGE,"E30.11.7.0");
            var Q225;
            Q225=sQuery(id+"F2.wireOp",EDGE,"E30.12.9.0");
            var Q226;
            Q226=sQuery(id+"F2.wireOp",EDGE,"E30.7.0.0");
            var Q227;
            Q227=sQuery(id+"F2.wireOp",EDGE,"E30.11.8.0");
            var Q228;
            Q228=sQuery(id+"F2.wireOp",EDGE,"E30.7.1.0");
            var Q229;
            Q229=sQuery(id+"F2.wireOp",EDGE,"E30.11.9.0");
            var Q230;
            Q230=sQuery(id+"F2.wireOp",EDGE,"E30.11.11.0");
            var Q231;
            Q231=sQuery(id+"F2.wireOp",EDGE,"E30.11.12.0");
            var Q232;
            Q232=sQuery(id+"F2.wireOp",EDGE,"E30.11.13.0");
            var Q233;
            Q233=sQuery(id+"F2.wireOp",EDGE,"E30.13.2.0");
            var Q234;
            Q234=sQuery(id+"F2.wireOp",EDGE,"E30.12.0.0");
            var Q235;
            Q235=sQuery(id+"F2.wireOp",EDGE,"E30.12.1.0");
            var Q236;
            Q236=sQuery(id+"F2.wireOp",EDGE,"E30.10.13.0");
            var Q237;
            Q237=sQuery(id+"F2.wireOp",EDGE,"E30.12.3.0");
            var Q238;
            Q238=sQuery(id+"F2.wireOp",EDGE,"E30.0.11.0");
            var Q239;
            Q239=sQuery(id+"F2.wireOp",EDGE,"E30.10.2.0");
            var Q240;
            Q240=sQuery(id+"F2.wireOp",EDGE,"E30.11.4.0");
            var Q241;
            Q241=sQuery(id+"F2.wireOp",EDGE,"E30.7.13.0");
            var Q242;
            Q242=sQuery(id+"F2.wireOp",EDGE,"E30.11.6.0");
            var Q243;
            Q243=sQuery(id+"F2.wireOp",EDGE,"E30.9.2.0");
            var Q244;
            Q244=sQuery(id+"F2.wireOp",EDGE,"E30.8.0.0");
            var Q245;
            Q245=sQuery(id+"F2.wireOp",EDGE,"E30.12.8.0");
            var Q246;
            Q246=sQuery(id+"F2.wireOp",EDGE,"E30.10.5.0");
            var Q247;
            Q247=sQuery(id+"F2.wireOp",EDGE,"E30.8.1.0");
            var Q248;
            Q248=sQuery(id+"F2.wireOp",EDGE,"E30.6.13.0");
            var Q249;
            Q249=sQuery(id+"F2.wireOp",EDGE,"E30.5.13.0");
            var Q250;
            Q250=sQuery(id+"F2.wireOp",EDGE,"E30.10.7.0");
            var Q251;
            Q251=sQuery(id+"F2.wireOp",EDGE,"E30.6.0.0");
            var Q252;
            Q252=sQuery(id+"F2.wireOp",EDGE,"E30.11.10.0");
            var Q253;
            Q253=sQuery(id+"F2.wireOp",EDGE,"E30.10.8.0");
            var Q254;
            Q254=sQuery(id+"F2.wireOp",EDGE,"E30.12.12.0");
            var Q255;
            Q255=sQuery(id+"F2.wireOp",EDGE,"E30.12.13.0");
            var Q256;
            Q256=sQuery(id+"F2.wireOp",EDGE,"E30.10.9.0");
            var Q257;
            Q257=sQuery(id+"F2.wireOp",EDGE,"E30.6.1.0");
            var Q258;
            Q258=sQuery(id+"F2.wireOp",EDGE,"E30.5.0.0");
            var Q259;
            Q259=sQuery(id+"F2.wireOp",EDGE,"E30.5.1.0");
            var Q260;
            Q260=sQuery(id+"F2.wireOp",EDGE,"E30.3.13.0");
            var Q261;
            Q261=sQuery(id+"F2.wireOp",EDGE,"E30.10.11.0");
            var Q262;
            Q262=sQuery(id+"F2.wireOp",EDGE,"E30.10.12.0");
            var Q263;
            Q263=sQuery(id+"F2.wireOp",EDGE,"E30.2.13.0");
            var Q264;
            Q264=sQuery(id+"F2.wireOp",EDGE,"E30.3.0.0");
            var Q265;
            Q265=sQuery(id+"F2.wireOp",EDGE,"E30.1.12.0");
            var Q266;
            Q266=sQuery(id+"F2.wireOp",EDGE,"E30.12.2.0");
            var Q267;
            Q267=sQuery(id+"F2.wireOp",EDGE,"E30.3.1.0");
            var Q268;
            Q268=sQuery(id+"F2.wireOp",EDGE,"E30.9.13.0");
            var Q269;
            Q269=sQuery(id+"F2.wireOp",EDGE,"E30.2.0.0");
            var Q270;
            Q270=sQuery(id+"F2.wireOp",EDGE,"E30.0.1.0");
            var Q271;
            Q271=sQuery(id+"F2.wireOp",EDGE,"E30.0.3.0");
            var Q272;
            Q272=sQuery(id+"F2.wireOp",EDGE,"E30.0.4.0");
            var Q273;
            Q273=sQuery(id+"F2.wireOp",EDGE,"E30.0.5.0");
            var Q274;
            Q274=sQuery(id+"F2.wireOp",EDGE,"E30.0.7.0");
            var Q275;
            Q275=sQuery(id+"F2.wireOp",EDGE,"E30.0.8.0");
            var Q276;
            Q276=sQuery(id+"F2.wireOp",EDGE,"E30.0.9.0");
            var Q277;
            Q277=sQuery(id+"F2.wireOp",EDGE,"E30.0.10.0");
            var Q278;
            Q278=sQuery(id+"F2.wireOp",EDGE,"E30.2.1.0");
            var Q279;
            Q279=sQuery(id+"F2.wireOp",EDGE,"E30.11.3.0");
            var Q280;
            Q280=sQuery(id+"F2.wireOp",EDGE,"E30.8.13.0");
            var Q281;
            Q281=sQuery(id+"F2.wireOp",EDGE,"E30.12.7.0");
            var Q282;
            Q282=sQuery(id+"F2.wireOp",EDGE,"E30.2.4.0");
            var Q283;
            Q283=sQuery(id+"F2.wireOp",EDGE,"E30.9.3.0");
            var Q284;
            Q284=sQuery(id+"F2.wireOp",EDGE,"E30.1.4.0");
            var Q285;
            Q285=sQuery(id+"F2.wireOp",EDGE,"E30.10.6.0");
            var Q286;
            Q286=sQuery(id+"F2.wireOp",EDGE,"E30.9.4.0");
            var Q287;
            Q287=sQuery(id+"F2.wireOp",EDGE,"E30.1.5.0");
            var Q288;
            Q288=sQuery(id+"F2.wireOp",EDGE,"E30.12.11.0");
            var Q289;
            Q289=sQuery(id+"F2.wireOp",EDGE,"E30.4.12.0");
            var Q290;
            Q290=sQuery(id+"F2.wireOp",EDGE,"E30.4.13.0");
            var Q291;
            Q291=sQuery(id+"F2.wireOp",EDGE,"E30.7.3.0");
            var Q292;
            Q292=sQuery(id+"F2.wireOp",EDGE,"E30.1.8.0");
            var Q293;
            Q293=sQuery(id+"F2.wireOp",EDGE,"E30.7.4.0");
            var Q294;
            Q294=sQuery(id+"F2.wireOp",EDGE,"E30.10.10.0");
            var Q295;
            Q295=sQuery(id+"F2.wireOp",EDGE,"E30.1.9.0");
            var Q296;
            Q296=sQuery(id+"F2.wireOp",EDGE,"E30.6.3.0");
            var Q297;
            Q297=sQuery(id+"F2.wireOp",EDGE,"E30.4.0.0");
            var Q298;
            Q298=sQuery(id+"F2.wireOp",EDGE,"E30.6.4.0");
            var Q299;
            Q299=sQuery(id+"F2.wireOp",EDGE,"E30.5.3.0");
            var Q300;
            Q300=sQuery(id+"F2.wireOp",EDGE,"E30.4.1.0");
            var Q301;
            Q301=sQuery(id+"F2.wireOp",EDGE,"E30.1.11.0");
            var Q302;
            Q302=sQuery(id+"F2.wireOp",EDGE,"E30.5.4.0");
            var Q303;
            Q303=sQuery(id+"F2.wireOp",EDGE,"E30.9.12.0");
            var Q304;
            Q304=sQuery(id+"F2.wireOp",EDGE,"E30.4.4.0");
            var Q305;
            Q305=sQuery(id+"F2.wireOp",EDGE,"E30.3.2.0");
            var Q306;
            Q306=sQuery(id+"F2.wireOp",EDGE,"E30.1.0.0");
            var Q307;
            Q307=sQuery(id+"F2.wireOp",EDGE,"E29");
            var Q308;
            Q308=sQuery(id+"F2.wireOp",EDGE,"E30.0.2.0");
            var Q309;
            Q309=sQuery(id+"F2.wireOp",EDGE,"E30.0.6.0");
            var Q310;
            Q310=sQuery(id+"F2.wireOp",EDGE,"E30.12.6.0");
            var Q311;
            Q311=sQuery(id+"F2.wireOp",EDGE,"E30.5.8.0");
            var Q312;
            Q312=sQuery(id+"F2.wireOp",EDGE,"E30.2.3.0");
            var Q313;
            Q313=sQuery(id+"F2.wireOp",EDGE,"E30.5.9.0");
            var Q314;
            Q314=sQuery(id+"F2.wireOp",EDGE,"E30.3.5.0");
            var Q315;
            Q315=sQuery(id+"F2.wireOp",EDGE,"E30.6.12.0");
            var Q316;
            Q316=sQuery(id+"F2.wireOp",EDGE,"E30.2.5.0");
            var Q317;
            Q317=sQuery(id+"F2.wireOp",EDGE,"E30.1.3.0");
            var Q318;
            Q318=sQuery(id+"F2.wireOp",EDGE,"E30.5.11.0");
            var Q319;
            Q319=sQuery(id+"F2.wireOp",EDGE,"E30.3.7.0");
            var Q320;
            Q320=sQuery(id+"F2.wireOp",EDGE,"E30.12.10.0");
            var Q321;
            Q321=sQuery(id+"F2.wireOp",EDGE,"E30.5.12.0");
            var Q322;
            Q322=sQuery(id+"F2.wireOp",EDGE,"E30.3.8.0");
            var Q323;
            Q323=sQuery(id+"F2.wireOp",EDGE,"E30.2.7.0");
            var Q324;
            Q324=sQuery(id+"F2.wireOp",EDGE,"E30.3.9.0");
            var Q325;
            Q325=sQuery(id+"F2.wireOp",EDGE,"E30.9.5.0");
            var Q326;
            Q326=sQuery(id+"F2.wireOp",EDGE,"E30.8.3.0");
            var Q327;
            Q327=sQuery(id+"F2.wireOp",EDGE,"E30.2.8.0");
            var Q328;
            Q328=sQuery(id+"F2.wireOp",EDGE,"E30.1.6.0");
            var Q329;
            Q329=sQuery(id+"F2.wireOp",EDGE,"E30.7.2.0");
            var Q330;
            Q330=sQuery(id+"F2.wireOp",EDGE,"E30.8.4.0");
            var Q331;
            Q331=sQuery(id+"F2.wireOp",EDGE,"E30.9.7.0");
            var Q332;
            Q332=sQuery(id+"F2.wireOp",EDGE,"E30.3.11.0");
            var Q333;
            Q333=sQuery(id+"F2.wireOp",EDGE,"E30.1.7.0");
            var Q334;
            Q334=sQuery(id+"F2.wireOp",EDGE,"E30.2.9.0");
            var Q335;
            Q335=sQuery(id+"F2.wireOp",EDGE,"E30.6.2.0");
            var Q336;
            Q336=sQuery(id+"F2.wireOp",EDGE,"E30.3.12.0");
            var Q337;
            Q337=sQuery(id+"F2.wireOp",EDGE,"E30.9.8.0");
            var Q338;
            Q338=sQuery(id+"F2.wireOp",EDGE,"E30.2.11.0");
            var Q339;
            Q339=sQuery(id+"F2.wireOp",EDGE,"E30.9.9.0");
            var Q340;
            Q340=sQuery(id+"F2.wireOp",EDGE,"E30.7.5.0");
            var Q341;
            Q341=sQuery(id+"F2.wireOp",EDGE,"E30.5.2.0");
            var Q342;
            Q342=sQuery(id+"F2.wireOp",EDGE,"E30.2.12.0");
            var Q343;
            Q343=sQuery(id+"F2.wireOp",EDGE,"E30.1.10.0");
            var Q344;
            Q344=sQuery(id+"F2.wireOp",EDGE,"E30.9.11.0");
            var Q345;
            Q345=sQuery(id+"F2.wireOp",EDGE,"E30.7.7.0");
            var Q346;
            Q346=sQuery(id+"F2.wireOp",EDGE,"E30.6.5.0");
            var Q347;
            Q347=sQuery(id+"F2.wireOp",EDGE,"E30.7.8.0");
            var Q348;
            Q348=sQuery(id+"F2.wireOp",EDGE,"E30.5.5.0");
            var Q349;
            Q349=sQuery(id+"F2.wireOp",EDGE,"E30.4.3.0");
            var Q350;
            Q350=sQuery(id+"F2.wireOp",EDGE,"E30.7.9.0");
            var Q351;
            Q351=sQuery(id+"F2.wireOp",EDGE,"E30.6.7.0");
            var Q352;
            Q352=sQuery(id+"F2.wireOp",EDGE,"E30.5.6.0");
            var Q353;
            Q353=sQuery(id+"F2.wireOp",EDGE,"E30.8.12.0");
            var Q354;
            Q354=sQuery(id+"F2.wireOp",EDGE,"E30.7.10.0");
            var Q355;
            Q355=sQuery(id+"F2.wireOp",EDGE,"E30.6.8.0");
            var Q356;
            Q356=sQuery(id+"F2.wireOp",EDGE,"E30.1.1.0");
            var Q357;
            Q357=sQuery(id+"F2.wireOp",EDGE,"E30.3.4.0");
            var Q358;
            Q358=sQuery(id+"F2.wireOp",EDGE,"E30.6.9.0");
            var Q359;
            Q359=sQuery(id+"F2.wireOp",EDGE,"E30.5.7.0");
            var Q360;
            Q360=sQuery(id+"F2.wireOp",EDGE,"E30.4.5.0");
            var Q361;
            Q361=sQuery(id+"F2.wireOp",EDGE,"E30.2.2.0");
            var Q362;
            Q362=sQuery(id+"F2.wireOp",EDGE,"E30.6.11.0");
            var Q363;
            Q363=sQuery(id+"F2.wireOp",EDGE,"E30.5.10.0");
            var Q364;
            Q364=sQuery(id+"F2.wireOp",EDGE,"E30.4.8.0");
            var Q365;
            Q365=sQuery(id+"F2.wireOp",EDGE,"E30.3.6.0");
            var Q366;
            Q366=sQuery(id+"F2.wireOp",EDGE,"E30.1.2.0");
            var Q367;
            Q367=sQuery(id+"F2.wireOp",EDGE,"E30.4.9.0");
            var Q368;
            Q368=sQuery(id+"F2.wireOp",EDGE,"E30.2.6.0");
            var Q369;
            Q369=sQuery(id+"F2.wireOp",EDGE,"E30.8.2.0");
            var Q370;
            Q370=sQuery(id+"F2.wireOp",EDGE,"E30.4.11.0");
            var Q371;
            Q371=sQuery(id+"F2.wireOp",EDGE,"E30.3.10.0");
            var Q372;
            Q372=sQuery(id+"F2.wireOp",EDGE,"E30.9.6.0");
            var Q373;
            Q373=sQuery(id+"F2.wireOp",EDGE,"E30.8.5.0");
            var Q374;
            Q374=sQuery(id+"F2.wireOp",EDGE,"E30.2.10.0");
            var Q375;
            Q375=sQuery(id+"F2.wireOp",EDGE,"E30.8.7.0");
            var Q376;
            Q376=sQuery(id+"F2.wireOp",EDGE,"E30.9.10.0");
            var Q377;
            Q377=sQuery(id+"F2.wireOp",EDGE,"E30.8.8.0");
            var Q378;
            Q378=sQuery(id+"F2.wireOp",EDGE,"E30.7.6.0");
            var Q379;
            Q379=sQuery(id+"F2.wireOp",EDGE,"E30.8.9.0");
            var Q380;
            Q380=sQuery(id+"F2.wireOp",EDGE,"E30.4.2.0");
            var Q381;
            Q381=sQuery(id+"F2.wireOp",EDGE,"E30.6.6.0");
            var Q382;
            Q382=sQuery(id+"F2.wireOp",EDGE,"E30.8.11.0");
            var Q383;
            Q383=sQuery(id+"F2.wireOp",EDGE,"E30.7.12.0");
            var Q384;
            Q384=sQuery(id+"F2.wireOp",EDGE,"E30.3.3.0");
            var Q385;
            Q385=sQuery(id+"F2.wireOp",EDGE,"E30.6.10.0");
            var Q386;
            Q386=sQuery(id+"F2.wireOp",EDGE,"E30.4.7.0");
            var Q387;
            Q387=sQuery(id+"F2.wireOp",EDGE,"E30.4.10.0");
            var Q388;
            Q388=sQuery(id+"F2.wireOp",EDGE,"E30.8.6.0");
            var Q389;
            Q389=sQuery(id+"F2.wireOp",EDGE,"E30.8.10.0");
            var Q390;
            Q390=sQuery(id+"F2.wireOp",EDGE,"E30.4.6.0");
            var Q391;
            Q391=sQuery(id+"F2.wireOp",EDGE,"E30.7.11.0");
            extrude(context, id + "F3", {"entities" : qUnion([Q0, Q1, Q2, Q3, Q4, Q5, Q6, Q7, Q8, Q9, Q10, Q11, Q12, Q13, Q14, Q15, Q16, Q17, Q18, Q19, Q20, Q21, Q22, Q23, Q24, Q25, Q26, Q27, Q28, Q29, Q30, Q31, Q32, Q33, Q34, Q35, Q36, Q37, Q38, Q39, Q40, Q41, Q42, Q43, Q44, Q45, Q46, Q47, Q48, Q49, Q50, Q51, Q52, Q53, Q54, Q55, Q56, Q57, Q58, Q59, Q60, Q61, Q62, Q63, Q64, Q65, Q66, Q67, Q68, Q69, Q70, Q71, Q72, Q73, Q74, Q75, Q76, Q77, Q78, Q79, Q80, Q81, Q82, Q83, Q84, Q85, Q86, Q87, Q88, Q89, Q90, Q91, Q92, Q93, Q94, Q95, Q96, Q97, Q98, Q99, Q100, Q101, Q102, Q103, Q104, Q105, Q106, Q107, Q108, Q109, Q110, Q111, Q112, Q113, Q114, Q115, Q116, Q117, Q118, Q119, Q120, Q121, Q122, Q123, Q124, Q125, Q126, Q127, Q128, Q129, Q130, Q131, Q132, Q133, Q134, Q135, Q136, Q137, Q138, Q139, Q140, Q141, Q142, Q143, Q144, Q145, Q146, Q147, Q148, Q149, Q150, Q151, Q152, Q153, Q154, Q155, Q156, Q157, Q158, Q159, Q160, Q161, Q162, Q163, Q164, Q165, Q166, Q167, Q168, Q169, Q170, Q171, Q172, Q173, Q174, Q175, Q176, Q177, Q178, Q179, Q180, Q181, Q182, Q183, Q184, Q185, Q186, Q187, Q188, Q189, Q190, Q191, Q192, Q193, Q194, Q195]), "surfaceEntities" : qUnion([Q196, Q197, Q198, Q199, Q200, Q201, Q202, Q203, Q204, Q205, Q206, Q207, Q208, Q209, Q210, Q211, Q212, Q213, Q214, Q215, Q216, Q217, Q218, Q219, Q220, Q221, Q222, Q223, Q224, Q225, Q226, Q227, Q228, Q229, Q230, Q231, Q232, Q233, Q234, Q235, Q236, Q237, Q238, Q239, Q240, Q241, Q242, Q243, Q244, Q245, Q246, Q247, Q248, Q249, Q250, Q251, Q252, Q253, Q254, Q255, Q256, Q257, Q258, Q259, Q260, Q261, Q262, Q263, Q264, Q265, Q266, Q267, Q268, Q269, Q270, Q271, Q272, Q273, Q274, Q275, Q276, Q277, Q278, Q279, Q280, Q281, Q282, Q283, Q284, Q285, Q286, Q287, Q288, Q289, Q290, Q291, Q292, Q293, Q294, Q295, Q296, Q297, Q298, Q299, Q300, Q301, Q302, Q303, Q304, Q305, Q306, Q307, Q308, Q309, Q310, Q311, Q312, Q313, Q314, Q315, Q316, Q317, Q318, Q319, Q320, Q321, Q322, Q323, Q324, Q325, Q326, Q327, Q328, Q329, Q330, Q331, Q332, Q333, Q334, Q335, Q336, Q337, Q338, Q339, Q340, Q341, Q342, Q343, Q344, Q345, Q346, Q347, Q348, Q349, Q350, Q351, Q352, Q353, Q354, Q355, Q356, Q357, Q358, Q359, Q360, Q361, Q362, Q363, Q364, Q365, Q366, Q367, Q368, Q369, Q370, Q371, Q372, Q373, Q374, Q375, Q376, Q377, Q378, Q379, Q380, Q381, Q382, Q383, Q384, Q385, Q386, Q387, Q388, Q389, Q390, Q391]), "depth" : 0.08 * mm});
        }
        {
            var Q0;
            Q0=qCreatedBy(makeId("Top.planeOp"),FACE);
            var sketch = newSketch(context, id + "F4", { "sketchPlane" : qUnion([Q0])});
            skLineSegment(sketch, "E31.bottom", {"start": v(3.5, 0) * mm, "end": v(41.8, 0) * mm});
            skLineSegment(sketch, "E31.top", {"start": v(3.5, 87.6) * mm, "end": v(41.8, 87.6) * mm});
            skLineSegment(sketch, "E31.left", {"start": v(0, 3.5) * mm, "end": v(0, 41.8) * mm});
            skLineSegment(sketch, "E31.right", {"start": v(87.6, 3.5) * mm, "end": v(87.6, 41.8) * mm});
            skPoint(sketch, "E32.visualSharp", {"position": v(0, 87.6) * mm});
            skArc(sketch, "E32.filletArc", {"start": v(3.5, 87.6) * mm, "mid": v(1.03, 86.57) * mm, "end": v(0, 84.1) * mm});
            skPoint(sketch, "E33.visualSharp", {"position": v(87.6, 87.6) * mm});
            skArc(sketch, "E33.filletArc", {"start": v(87.6, 84.1) * mm, "mid": v(86.57, 86.57) * mm, "end": v(84.1, 87.6) * mm});
            skPoint(sketch, "E34.visualSharp", {"position": v(87.6, 0) * mm});
            skArc(sketch, "E34.filletArc", {"start": v(84.1, 0) * mm, "mid": v(86.57, 1.03) * mm, "end": v(87.6, 3.5) * mm});
            skPoint(sketch, "E35.visualSharp", {"position": v(0, 0) * mm});
            skArc(sketch, "E35.filletArc", {"start": v(0, 3.5) * mm, "mid": v(1.03, 1.03) * mm, "end": v(3.5, 0) * mm});
            skLineSegment(sketch, "E36.0", {"start": v(3.8, 85.55) * mm, "end": v(41.8, 85.55) * mm});
            skLineSegment(sketch, "E36.1", {"start": v(2.05, 3.8) * mm, "end": v(2.05, 41.8) * mm});
            skLineSegment(sketch, "E36.2", {"start": v(3.8, 2.05) * mm, "end": v(41.8, 2.05) * mm});
            skLineSegment(sketch, "E36.3", {"start": v(85.55, 3.8) * mm, "end": v(85.55, 41.8) * mm});
            skPoint(sketch, "E37.visualSharp", {"position": v(2.05, 85.55) * mm});
            skArc(sketch, "E37.filletArc", {"start": v(3.8, 85.55) * mm, "mid": v(2.56, 85.04) * mm, "end": v(2.05, 83.8) * mm});
            skPoint(sketch, "E38.visualSharp", {"position": v(85.55, 85.55) * mm});
            skArc(sketch, "E38.filletArc", {"start": v(85.55, 83.8) * mm, "mid": v(85.04, 85.04) * mm, "end": v(83.8, 85.55) * mm});
            skPoint(sketch, "E39.visualSharp", {"position": v(2.05, 2.05) * mm});
            skArc(sketch, "E39.filletArc", {"start": v(2.05, 3.8) * mm, "mid": v(2.56, 2.56) * mm, "end": v(3.8, 2.05) * mm});
            skPoint(sketch, "E40.visualSharp", {"position": v(85.55, 2.05) * mm});
            skArc(sketch, "E40.filletArc", {"start": v(83.8, 2.05) * mm, "mid": v(85.04, 2.56) * mm, "end": v(85.55, 3.8) * mm});
            skLineSegment(sketch, "E41", {"start": v(0, 43.8) * mm, "end": v(43.8, 43.8) * mm, "construction": true});
            skPoint(sketch, "E41.endSnap0", {"position": v(0, 43.8) * mm});
            skLineSegment(sketch, "E42", {"start": v(43.8, 2.05) * mm, "end": v(43.8, 43.8) * mm, "construction": true});
            skLineSegment(sketch, "E43", {"start": v(41.8, 2.05) * mm, "end": v(41.8, 0) * mm});
            skLineSegment(sketch, "E44", {"start": v(45.8, 0) * mm, "end": v(45.8, 2.05) * mm});
            skLineSegment(sketch, "E45.trimOffspring", {"start": v(45.8, 0) * mm, "end": v(84.1, 0) * mm});
            skLineSegment(sketch, "E46.trimOffspring", {"start": v(45.8, 2.05) * mm, "end": v(83.8, 2.05) * mm});
            skLineSegment(sketch, "E47", {"start": v(41.8, 85.55) * mm, "end": v(41.8, 87.6) * mm});
            skLineSegment(sketch, "E48", {"start": v(45.8, 85.55) * mm, "end": v(45.8, 87.6) * mm});
            skLineSegment(sketch, "E49.trimOffspring", {"start": v(45.8, 85.55) * mm, "end": v(83.8, 85.55) * mm});
            skLineSegment(sketch, "E50.trimOffspring", {"start": v(45.8, 87.6) * mm, "end": v(84.1, 87.6) * mm});
            skLineSegment(sketch, "E51", {"start": v(0, 45.8) * mm, "end": v(2.05, 45.8) * mm});
            skLineSegment(sketch, "E52", {"start": v(0, 41.8) * mm, "end": v(2.05, 41.8) * mm});
            skLineSegment(sketch, "E53.trimOffspring", {"start": v(2.05, 45.8) * mm, "end": v(2.05, 83.8) * mm});
            skLineSegment(sketch, "E54.trimOffspring", {"start": v(0, 45.8) * mm, "end": v(0, 84.1) * mm});
            skLineSegment(sketch, "E55", {"start": v(85.55, 45.8) * mm, "end": v(87.6, 45.8) * mm});
            skLineSegment(sketch, "E56", {"start": v(85.55, 41.8) * mm, "end": v(87.6, 41.8) * mm});
            skLineSegment(sketch, "E57.trimOffspring", {"start": v(85.55, 45.8) * mm, "end": v(85.55, 83.8) * mm});
            skLineSegment(sketch, "E58.trimOffspring", {"start": v(87.6, 45.8) * mm, "end": v(87.6, 84.1) * mm});
            skLineSegment(sketch, "E59", {"start": v(91.6, 49.8) * mm, "end": v(98.6, 49.8) * mm});
            skLineSegment(sketch, "E60", {"start": v(98.6, 49.8) * mm, "end": v(98.6, 37.8) * mm});
            skLineSegment(sketch, "E61", {"start": v(98.6, 37.8) * mm, "end": v(91.6, 37.8) * mm});
            skLineSegment(sketch, "E62", {"start": v(37.8, -4) * mm, "end": v(37.8, -11) * mm});
            skLineSegment(sketch, "E63", {"start": v(37.8, -11) * mm, "end": v(49.8, -11) * mm});
            skLineSegment(sketch, "E64", {"start": v(49.8, -11) * mm, "end": v(49.8, -4) * mm});
            skLineSegment(sketch, "E65", {"start": v(-4, 49.8) * mm, "end": v(-11, 49.8) * mm});
            skLineSegment(sketch, "E66", {"start": v(-11, 49.8) * mm, "end": v(-11, 37.8) * mm});
            skLineSegment(sketch, "E67", {"start": v(-11, 37.8) * mm, "end": v(-4, 37.8) * mm});
            skLineSegment(sketch, "E68", {"start": v(37.8, 91.6) * mm, "end": v(37.8, 98.6) * mm});
            skLineSegment(sketch, "E69", {"start": v(37.8, 98.6) * mm, "end": v(49.8, 98.6) * mm});
            skLineSegment(sketch, "E70", {"start": v(49.8, 98.6) * mm, "end": v(49.8, 91.6) * mm});
            skLineSegment(sketch, "E71", {"start": v(37.8, 91.6) * mm, "end": v(39.3, 91.6) * mm});
            skLineSegment(sketch, "E72", {"start": v(39.3, 91.6) * mm, "end": v(39.3, 92.85) * mm});
            skLineSegment(sketch, "E73", {"start": v(39.3, 92.85) * mm, "end": v(41.3, 92.85) * mm});
            skLineSegment(sketch, "E74", {"start": v(41.3, 92.85) * mm, "end": v(41.3, 91.6) * mm});
            skLineSegment(sketch, "E75", {"start": v(41.3, 91.6) * mm, "end": v(42.8, 91.6) * mm});
            skLineSegment(sketch, "E76", {"start": v(42.8, 91.6) * mm, "end": v(42.8, 92.85) * mm});
            skLineSegment(sketch, "E77", {"start": v(42.8, 92.85) * mm, "end": v(44.8, 92.85) * mm});
            skLineSegment(sketch, "E78", {"start": v(44.8, 92.85) * mm, "end": v(44.8, 91.6) * mm});
            skLineSegment(sketch, "E79", {"start": v(44.8, 91.6) * mm, "end": v(46.3, 91.6) * mm});
            skLineSegment(sketch, "E80", {"start": v(46.3, 91.6) * mm, "end": v(46.3, 92.85) * mm});
            skLineSegment(sketch, "E81", {"start": v(46.3, 92.85) * mm, "end": v(48.3, 92.85) * mm});
            skLineSegment(sketch, "E82", {"start": v(48.3, 92.85) * mm, "end": v(48.3, 91.6) * mm});
            skLineSegment(sketch, "E83", {"start": v(48.3, 91.6) * mm, "end": v(49.8, 91.6) * mm});
            skLineSegment(sketch, "E84", {"start": v(91.6, 49.8) * mm, "end": v(91.6, 48.3) * mm});
            skLineSegment(sketch, "E85", {"start": v(91.6, 48.3) * mm, "end": v(92.85, 48.3) * mm});
            skLineSegment(sketch, "E86", {"start": v(92.85, 48.3) * mm, "end": v(92.85, 46.3) * mm});
            skLineSegment(sketch, "E87", {"start": v(92.85, 46.3) * mm, "end": v(91.6, 46.3) * mm});
            skLineSegment(sketch, "E88", {"start": v(91.6, 46.3) * mm, "end": v(91.6, 44.8) * mm});
            skLineSegment(sketch, "E89", {"start": v(91.6, 44.8) * mm, "end": v(92.85, 44.8) * mm});
            skLineSegment(sketch, "E90", {"start": v(92.85, 44.8) * mm, "end": v(92.85, 42.8) * mm});
            skLineSegment(sketch, "E91", {"start": v(92.85, 42.8) * mm, "end": v(91.6, 42.8) * mm});
            skLineSegment(sketch, "E92", {"start": v(91.6, 42.8) * mm, "end": v(91.6, 41.3) * mm});
            skLineSegment(sketch, "E93", {"start": v(91.6, 41.3) * mm, "end": v(92.85, 41.3) * mm});
            skLineSegment(sketch, "E94", {"start": v(92.85, 41.3) * mm, "end": v(92.85, 39.3) * mm});
            skLineSegment(sketch, "E95", {"start": v(92.85, 39.3) * mm, "end": v(91.6, 39.3) * mm});
            skLineSegment(sketch, "E96", {"start": v(91.6, 39.3) * mm, "end": v(91.6, 37.8) * mm});
            skLineSegment(sketch, "E97", {"start": v(49.8, -4) * mm, "end": v(48.2, -4) * mm});
            skLineSegment(sketch, "E98", {"start": v(48.2, -4) * mm, "end": v(48.2, -5.25) * mm});
            skLineSegment(sketch, "E99", {"start": v(48.2, -5.25) * mm, "end": v(46.43, -5.25) * mm});
            skLineSegment(sketch, "E100", {"start": v(46.43, -5.25) * mm, "end": v(46.43, -4) * mm});
            skLineSegment(sketch, "E101", {"start": v(46.43, -4) * mm, "end": v(44.54, -4) * mm});
            skLineSegment(sketch, "E102", {"start": v(44.54, -4) * mm, "end": v(44.54, -5.25) * mm});
            skLineSegment(sketch, "E103", {"start": v(44.54, -5.25) * mm, "end": v(42.7, -5.25) * mm});
            skLineSegment(sketch, "E104", {"start": v(42.7, -5.25) * mm, "end": v(42.7, -4) * mm});
            skLineSegment(sketch, "E105", {"start": v(42.7, -4) * mm, "end": v(41.06, -4) * mm});
            skLineSegment(sketch, "E106", {"start": v(41.06, -4) * mm, "end": v(41.06, -5.25) * mm});
            skLineSegment(sketch, "E107", {"start": v(41.06, -5.25) * mm, "end": v(38.85, -5.25) * mm});
            skLineSegment(sketch, "E108", {"start": v(38.85, -5.25) * mm, "end": v(38.85, -4) * mm});
            skLineSegment(sketch, "E109", {"start": v(38.85, -4) * mm, "end": v(37.8, -4) * mm});
            skLineSegment(sketch, "E110", {"start": v(-4, 37.8) * mm, "end": v(-4, 39.3) * mm});
            skLineSegment(sketch, "E111", {"start": v(-4, 39.3) * mm, "end": v(-5.25, 39.3) * mm});
            skLineSegment(sketch, "E112", {"start": v(-5.25, 39.3) * mm, "end": v(-5.25, 41.3) * mm});
            skLineSegment(sketch, "E113", {"start": v(-5.25, 41.3) * mm, "end": v(-4, 41.3) * mm});
            skLineSegment(sketch, "E114", {"start": v(-4, 41.3) * mm, "end": v(-4, 42.8) * mm});
            skLineSegment(sketch, "E115", {"start": v(-4, 42.8) * mm, "end": v(-5.25, 42.8) * mm});
            skLineSegment(sketch, "E116", {"start": v(-5.25, 42.8) * mm, "end": v(-5.25, 44.8) * mm});
            skLineSegment(sketch, "E117", {"start": v(-5.25, 44.8) * mm, "end": v(-4, 44.8) * mm});
            skLineSegment(sketch, "E118", {"start": v(-4, 44.8) * mm, "end": v(-4, 46.3) * mm});
            skLineSegment(sketch, "E119", {"start": v(-4, 46.3) * mm, "end": v(-5.25, 46.3) * mm});
            skLineSegment(sketch, "E120", {"start": v(-5.25, 46.3) * mm, "end": v(-5.25, 48.3) * mm});
            skLineSegment(sketch, "E121", {"start": v(-5.25, 48.3) * mm, "end": v(-4, 48.3) * mm});
            skLineSegment(sketch, "E122", {"start": v(-4, 48.3) * mm, "end": v(-4, 49.8) * mm});
            skSolve(sketch);
        }
        {
            var Q0;
            Q0=makeQuery(id+"F4.imprint","IMPRINT",FACE,{"disambiguationData":[TD([[makeQuery(id+"F4.imprint","IMPRINT",EDGE,{"derivedFrom":sQuery(id+"F4.wireOp",EDGE,"E68")}),-1.0]])]});
            var Q1;
            Q1=makeQuery(id+"F4.imprint","IMPRINT",FACE,{"disambiguationData":[TD([[makeQuery(id+"F4.imprint","IMPRINT",EDGE,{"derivedFrom":sQuery(id+"F4.wireOp",EDGE,"E59")}),-1.0]])]});
            var Q2;
            Q2=makeQuery(id+"F4.imprint","IMPRINT",FACE,{"disambiguationData":[TD([[makeQuery(id+"F4.imprint","IMPRINT",EDGE,{"derivedFrom":sQuery(id+"F4.wireOp",EDGE,"E65")}),1.0]])]});
            var Q3;
            Q3=makeQuery(id+"F4.imprint","IMPRINT",FACE,{"disambiguationData":[TD([[makeQuery(id+"F4.imprint","IMPRINT",EDGE,{"derivedFrom":sQuery(id+"F4.wireOp",EDGE,"E31.right")}),1.0]])]});
            var Q4;
            Q4=makeQuery(id+"F4.imprint","IMPRINT",FACE,{"disambiguationData":[TD([[makeQuery(id+"F4.imprint","IMPRINT",EDGE,{"derivedFrom":sQuery(id+"F4.wireOp",EDGE,"E33.filletArc")}),1.0]])]});
            var Q5;
            Q5=makeQuery(id+"F4.imprint","IMPRINT",FACE,{"disambiguationData":[TD([[makeQuery(id+"F4.imprint","IMPRINT",EDGE,{"derivedFrom":sQuery(id+"F4.wireOp",EDGE,"E62")}),1.0]])]});
            var Q6;
            Q6=makeQuery(id+"F4.imprint","IMPRINT",FACE,{"disambiguationData":[TD([[makeQuery(id+"F4.imprint","IMPRINT",EDGE,{"derivedFrom":sQuery(id+"F4.wireOp",EDGE,"E31.top")}),-1.0]])]});
            var Q7;
            Q7=makeQuery(id+"F4.imprint","IMPRINT",FACE,{"disambiguationData":[TD([[makeQuery(id+"F4.imprint","IMPRINT",EDGE,{"derivedFrom":sQuery(id+"F4.wireOp",EDGE,"E31.bottom")}),1.0]])]});
            extrude(context, id + "F5", {"entities" : qUnion([Q0, Q1, Q2, Q3, Q4, Q5, Q6, Q7]), "depth" : .508 * mm});
        }
        {
            var Q0;
            Q0=qCreatedBy(makeId("Top.planeOp"),FACE);
            var sketch = newSketch(context, id + "F6", { "sketchPlane" : qUnion([Q0])});
            skLineSegment(sketch, "E123.bottom", {"start": v(3.5, 0) * mm, "end": v(84.1, 0) * mm});
            skLineSegment(sketch, "E123.top", {"start": v(3.5, 87.6) * mm, "end": v(84.1, 87.6) * mm});
            skLineSegment(sketch, "E123.left", {"start": v(0, 3.5) * mm, "end": v(0, 84.1) * mm});
            skLineSegment(sketch, "E123.right", {"start": v(87.6, 3.5) * mm, "end": v(87.6, 84.1) * mm});
            skPoint(sketch, "E124.visualSharp", {"position": v(0, 87.6) * mm});
            skArc(sketch, "E124.filletArc", {"start": v(3.5, 87.6) * mm, "mid": v(1.03, 86.57) * mm, "end": v(0, 84.1) * mm});
            skPoint(sketch, "E125.visualSharp", {"position": v(0, 0) * mm});
            skArc(sketch, "E125.filletArc", {"start": v(0, 3.5) * mm, "mid": v(1.03, 1.03) * mm, "end": v(3.5, 0) * mm});
            skPoint(sketch, "E126.visualSharp", {"position": v(87.6, 0) * mm});
            skArc(sketch, "E126.filletArc", {"start": v(84.1, 0) * mm, "mid": v(86.57, 1.03) * mm, "end": v(87.6, 3.5) * mm});
            skPoint(sketch, "E127.visualSharp", {"position": v(87.6, 87.6) * mm});
            skArc(sketch, "E127.filletArc", {"start": v(87.6, 84.1) * mm, "mid": v(86.57, 86.57) * mm, "end": v(84.1, 87.6) * mm});
            skSolve(sketch);
        }
        {
            var Q0;
            Q0 = qSketchRegion(id + "F6", true);
            extrude(context, id + "F7", {"entities" : qUnion([Q0]), "oppositeDirection" : true, "depth" : .125 * mm});
        }
    });
